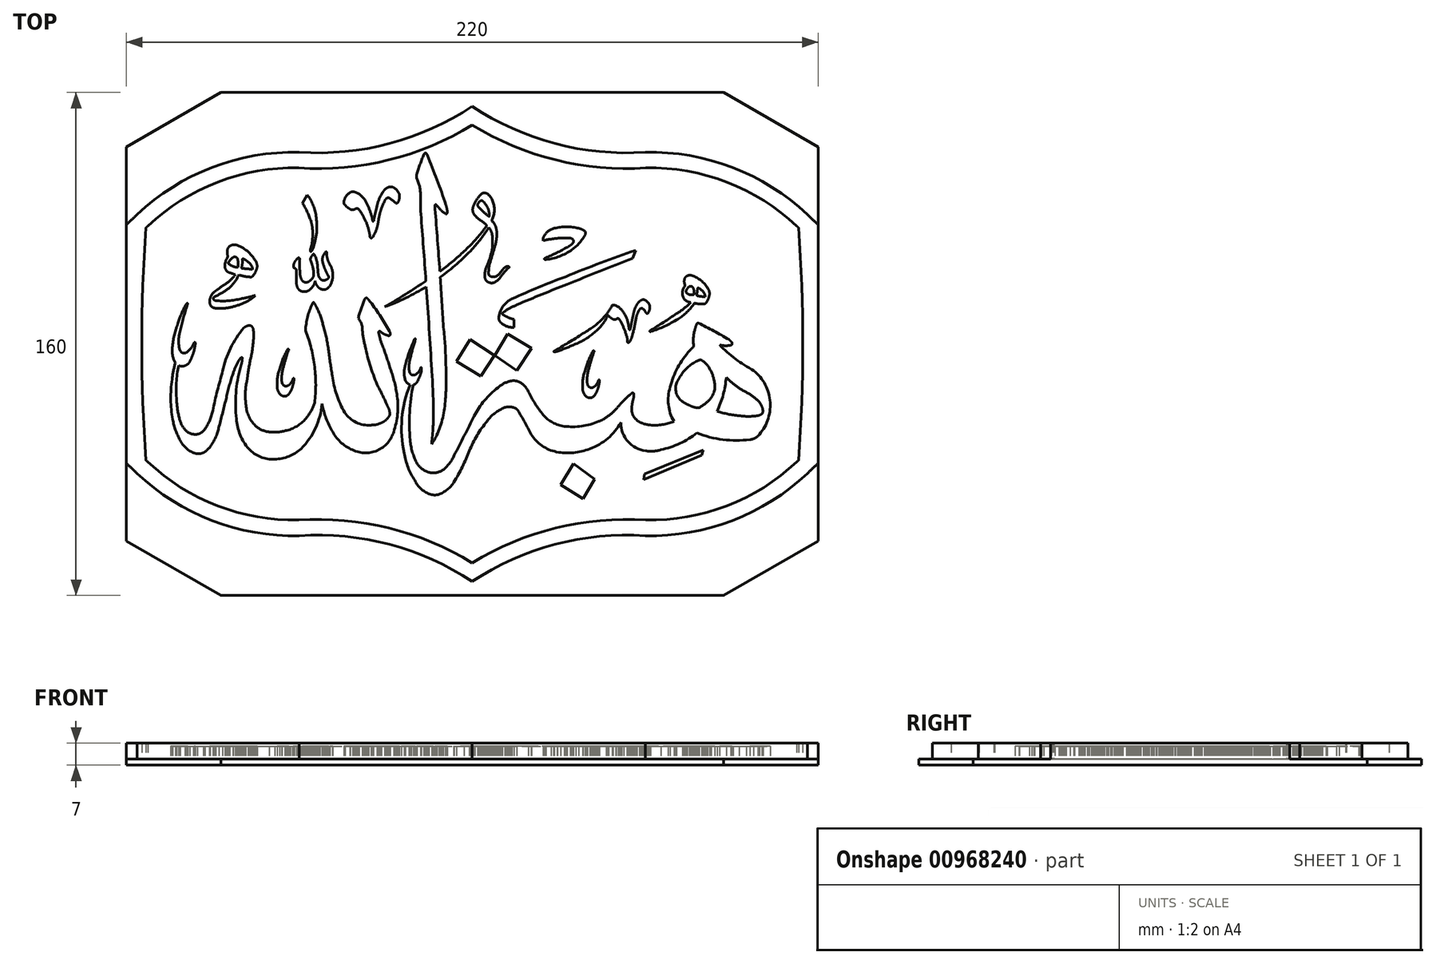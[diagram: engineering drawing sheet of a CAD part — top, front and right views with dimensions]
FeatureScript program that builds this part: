
annotation { "Feature Type Name" : "Feature", "Feature Type Description" : "" }
export const myFeature = defineFeature(function(context is Context, id is Id, definition is map)
    precondition{}
    {
        {
            var Q0;
            Q0=qCreatedBy(makeId("Top.planeOp"),FACE);
            var sketch = newSketch(context, id + "F0", { "sketchPlane" : qUnion([Q0])});
            skLineSegment(sketch, "E0.bottom", {"start": v(-104.12, 78.93) * mm, "end": v(115.88, 78.93) * mm});
            skLineSegment(sketch, "E0.top", {"start": v(-104.12, -81.07) * mm, "end": v(115.88, -81.07) * mm});
            skLineSegment(sketch, "E0.left", {"start": v(-104.12, 78.93) * mm, "end": v(-104.12, -81.07) * mm});
            skLineSegment(sketch, "E0.right", {"start": v(115.88, 78.93) * mm, "end": v(115.88, -81.07) * mm});
            skSolve(sketch);
        }
        {
            var Q0;
            Q0 = qSketchRegion(id + "F0", true);
            extrude(context, id + "F1", {"entities" : qUnion([Q0]), "oppositeDirection" : true, "depth" : 2 * mm, "offsetDistance" : 25 * mm});
        }
        {
            var Q0;
            Q0=makeQuery(id+"F1.opExtrude","CAP_FACE",FACE,{"disambiguationData":[OSD([sQuery(id+"F0.wireOp",EDGE,"E0.bottom"),sQuery(id+"F0.wireOp",EDGE,"E0.top"),sQuery(id+"F0.wireOp",EDGE,"E0.left"),sQuery(id+"F0.wireOp",EDGE,"E0.right")])],"isStart":true});
            var sketch = newSketch(context, id + "F2", { "sketchPlane" : qUnion([Q0])});
            skArc(sketch, "E1", {"start": v(87.55, 0.3) * mm, "mid": v(82.74, 3.05) * mm, "end": v(77.8, 5.57) * mm});
            skArc(sketch, "E2", {"start": v(88.37, -0.47) * mm, "mid": v(88.17, -0.23) * mm, "end": v(87.95, 0) * mm});
            skArc(sketch, "E3", {"start": v(88.17, -1.46) * mm, "mid": v(88.52, -1.04) * mm, "end": v(88.4, -0.5) * mm});
            skArc(sketch, "E4", {"start": v(84.5, -1.3) * mm, "mid": v(86.32, -1.62) * mm, "end": v(88.17, -1.46) * mm});
            skPoint(sketch, "E5.visualSharp", {"position": v(88.39, -0.49) * mm});
            skArc(sketch, "E5.filletArc", {"start": v(88.37, -0.47) * mm, "mid": v(88.38, -0.48) * mm, "end": v(88.4, -0.5) * mm});
            skPoint(sketch, "E6.visualSharp", {"position": v(87.75, 0.19) * mm});
            skArc(sketch, "E6.filletArc", {"start": v(87.95, 0) * mm, "mid": v(87.76, 0.17) * mm, "end": v(87.55, 0.3) * mm});
            skArc(sketch, "E7", {"start": v(84.5, -1.3) * mm, "mid": v(89.64, -5.83) * mm, "end": v(95.4, -9.52) * mm});
            skArc(sketch, "E8", {"start": v(96.73, -30.37) * mm, "mid": v(100.63, -19.66) * mm, "end": v(95.4, -9.52) * mm});
            skArc(sketch, "E9", {"start": v(94.18, -31.5) * mm, "mid": v(95.5, -31.19) * mm, "end": v(96.63, -30.46) * mm});
            skArc(sketch, "E10", {"start": v(77.35, -29.37) * mm, "mid": v(85.63, -31.5) * mm, "end": v(94.18, -31.5) * mm});
            skPoint(sketch, "E11.visualSharp", {"position": v(96.69, -30.4) * mm});
            skArc(sketch, "E11.filletArc", {"start": v(96.63, -30.46) * mm, "mid": v(96.68, -30.41) * mm, "end": v(96.73, -30.37) * mm});
            skArc(sketch, "E12", {"start": v(65.9, -34.73) * mm, "mid": v(71.92, -32.7) * mm, "end": v(77.35, -29.37) * mm});
            skArc(sketch, "E13", {"start": v(61.07, -35.07) * mm, "mid": v(63.5, -35.19) * mm, "end": v(65.9, -34.73) * mm});
            skArc(sketch, "E14", {"start": v(53.13, -26.05) * mm, "mid": v(55.36, -32.08) * mm, "end": v(61.07, -35.07) * mm});
            skArc(sketch, "E15", {"start": v(43.34, -34.38) * mm, "mid": v(49, -31.11) * mm, "end": v(53.13, -26.05) * mm});
            skArc(sketch, "E16", {"start": v(32.67, -35.4) * mm, "mid": v(38.08, -35.68) * mm, "end": v(43.34, -34.38) * mm});
            skArc(sketch, "E17", {"start": v(24.64, -29.8) * mm, "mid": v(28.07, -33.44) * mm, "end": v(32.67, -35.4) * mm});
            skArc(sketch, "E18", {"start": v(24.64, -29.8) * mm, "mid": v(22.58, -25.96) * mm, "end": v(20.37, -22.21) * mm});
            skArc(sketch, "E19", {"start": v(19.47, -21.43) * mm, "mid": v(17.35, -21.06) * mm, "end": v(15.29, -21.72) * mm});
            skPoint(sketch, "E20.visualSharp", {"position": v(20.09, -21.76) * mm});
            skArc(sketch, "E20.filletArc", {"start": v(20.37, -22.21) * mm, "mid": v(19.98, -21.75) * mm, "end": v(19.47, -21.43) * mm});
            skArc(sketch, "E21", {"start": v(15.13, -21.8) * mm, "mid": v(12.63, -23.44) * mm, "end": v(10.6, -25.64) * mm});
            skPoint(sketch, "E22.visualSharp", {"position": v(15.22, -21.76) * mm});
            skArc(sketch, "E22.filletArc", {"start": v(15.13, -21.8) * mm, "mid": v(15.2, -21.76) * mm, "end": v(15.29, -21.72) * mm});
            skArc(sketch, "E23", {"start": v(10.6, -25.64) * mm, "mid": v(7.43, -30.14) * mm, "end": v(4.98, -35.06) * mm});
            skArc(sketch, "E24", {"start": v(0.03, -45.08) * mm, "mid": v(2.73, -40.18) * mm, "end": v(4.98, -35.06) * mm});
            skArc(sketch, "E25", {"start": v(-4.78, -48.95) * mm, "mid": v(-2.07, -47.4) * mm, "end": v(0.03, -45.08) * mm});
            skArc(sketch, "E26", {"start": v(-7.84, -48.76) * mm, "mid": v(-6.32, -49.1) * mm, "end": v(-4.78, -48.95) * mm});
            skArc(sketch, "E27", {"start": v(-12.37, -44.5) * mm, "mid": v(-10.52, -47.06) * mm, "end": v(-7.84, -48.76) * mm});
            skArc(sketch, "E28", {"start": v(-15.76, -35.82) * mm, "mid": v(-14.54, -40.34) * mm, "end": v(-12.37, -44.5) * mm});
            skArc(sketch, "E29", {"start": v(-13.88, -14.04) * mm, "mid": v(-16.5, -24.78) * mm, "end": v(-15.76, -35.82) * mm});
            skArc(sketch, "E30", {"start": v(-12.91, -14.04) * mm, "mid": v(-14.05, -22.82) * mm, "end": v(-13.88, -31.68) * mm});
            skArc(sketch, "E31", {"start": v(-13.88, -31.68) * mm, "mid": v(-13.2, -35.34) * mm, "end": v(-11.83, -38.8) * mm});
            skArc(sketch, "E32", {"start": v(-11.83, -38.8) * mm, "mid": v(-10.17, -40.72) * mm, "end": v(-7.92, -41.89) * mm});
            skArc(sketch, "E33", {"start": v(-7.92, -41.89) * mm, "mid": v(-5.67, -42.02) * mm, "end": v(-3.57, -41.21) * mm});
            skArc(sketch, "E34", {"start": v(-3.57, -41.21) * mm, "mid": v(-1.39, -39.11) * mm, "end": v(0.12, -36.5) * mm});
            skArc(sketch, "E35", {"start": v(0.12, -36.5) * mm, "mid": v(3.34, -30.27) * mm, "end": v(6.43, -24) * mm});
            skArc(sketch, "E36", {"start": v(14.07, -14.96) * mm, "mid": v(9.76, -19.06) * mm, "end": v(6.43, -24) * mm});
            skArc(sketch, "E37", {"start": v(18.04, -12.86) * mm, "mid": v(15.91, -13.65) * mm, "end": v(14.07, -14.96) * mm});
            skArc(sketch, "E38", {"start": v(20, -12.86) * mm, "mid": v(19.02, -12.76) * mm, "end": v(18.04, -12.86) * mm});
            skArc(sketch, "E39", {"start": v(23.7, -16.2) * mm, "mid": v(22.24, -14.1) * mm, "end": v(20, -12.86) * mm});
            skArc(sketch, "E40", {"start": v(23.7, -16.2) * mm, "mid": v(25.88, -20.07) * mm, "end": v(28.48, -23.66) * mm});
            skArc(sketch, "E41", {"start": v(28.48, -23.66) * mm, "mid": v(31.47, -26.06) * mm, "end": v(35.1, -27.27) * mm});
            skArc(sketch, "E42", {"start": v(35.1, -27.27) * mm, "mid": v(40.7, -27.2) * mm, "end": v(46.1, -25.73) * mm});
            skArc(sketch, "E43", {"start": v(46.1, -25.73) * mm, "mid": v(47.63, -25.01) * mm, "end": v(49.03, -24.08) * mm});
            skArc(sketch, "E44", {"start": v(49.03, -24.08) * mm, "mid": v(50.8, -22.64) * mm, "end": v(52.33, -20.96) * mm});
            skArc(sketch, "E45", {"start": v(56.14, -17.16) * mm, "mid": v(54.15, -18.98) * mm, "end": v(52.33, -20.96) * mm});
            skArc(sketch, "E46", {"start": v(56.66, -16.72) * mm, "mid": v(56.4, -16.93) * mm, "end": v(56.14, -17.16) * mm});
            skArc(sketch, "E47", {"start": v(57.07, -16.66) * mm, "mid": v(56.86, -16.63) * mm, "end": v(56.66, -16.72) * mm});
            skArc(sketch, "E48", {"start": v(57.27, -16.98) * mm, "mid": v(57.22, -16.79) * mm, "end": v(57.07, -16.66) * mm});
            skArc(sketch, "E49", {"start": v(57.12, -18.64) * mm, "mid": v(57.26, -17.82) * mm, "end": v(57.27, -16.98) * mm});
            skArc(sketch, "E50", {"start": v(57.12, -18.64) * mm, "mid": v(56.72, -20.33) * mm, "end": v(56.61, -22.06) * mm});
            skArc(sketch, "E51", {"start": v(56.61, -22.06) * mm, "mid": v(56.83, -23.28) * mm, "end": v(57.4, -24.37) * mm});
            skArc(sketch, "E52", {"start": v(57.4, -24.37) * mm, "mid": v(58.21, -25.3) * mm, "end": v(59.23, -25.97) * mm});
            skArc(sketch, "E53", {"start": v(59.23, -25.97) * mm, "mid": v(60.8, -26.56) * mm, "end": v(62.45, -26.84) * mm});
            skArc(sketch, "E54", {"start": v(62.45, -26.84) * mm, "mid": v(66.32, -26.75) * mm, "end": v(70.03, -25.68) * mm});
            skArc(sketch, "E55", {"start": v(68.83, -14.8) * mm, "mid": v(68.28, -20.36) * mm, "end": v(70.03, -25.68) * mm});
            skArc(sketch, "E56", {"start": v(75.09, -3.13) * mm, "mid": v(71.25, -8.58) * mm, "end": v(68.83, -14.8) * mm});
            skArc(sketch, "E57", {"start": v(76.33, -1.87) * mm, "mid": v(75.7, -2.48) * mm, "end": v(75.09, -3.13) * mm});
            skArc(sketch, "E58", {"start": v(76.74, 3.66) * mm, "mid": v(76.23, 0.92) * mm, "end": v(76.33, -1.87) * mm});
            skArc(sketch, "E59", {"start": v(77.32, 5.35) * mm, "mid": v(77, 4.52) * mm, "end": v(76.74, 3.66) * mm});
            skArc(sketch, "E60", {"start": v(77.8, 5.57) * mm, "mid": v(77.51, 5.57) * mm, "end": v(77.32, 5.35) * mm});
            skArc(sketch, "E61", {"start": v(77.95, -6.25) * mm, "mid": v(74.7, -8.26) * mm, "end": v(72.19, -11.13) * mm});
            skArc(sketch, "E62", {"start": v(72.14, -11.2) * mm, "mid": v(71.55, -12.18) * mm, "end": v(71.03, -13.2) * mm});
            skPoint(sketch, "E63.visualSharp", {"position": v(76.34, -7.08) * mm});
            skArc(sketch, "E63.filletArc", {"start": v(72.14, -11.2) * mm, "mid": v(72.17, -11.16) * mm, "end": v(72.19, -11.13) * mm});
            skArc(sketch, "E64", {"start": v(72.68, -19.35) * mm, "mid": v(73.84, -20.07) * mm, "end": v(75.08, -20.64) * mm});
            skPoint(sketch, "E65.visualSharp", {"position": v(69.96, -16.58) * mm});
            skArc(sketch, "E65.filletArc", {"start": v(71.03, -13.2) * mm, "mid": v(70.75, -16.57) * mm, "end": v(72.68, -19.35) * mm});
            skArc(sketch, "E66", {"start": v(75.08, -20.64) * mm, "mid": v(76.06, -21.05) * mm, "end": v(77.08, -21.32) * mm});
            skArc(sketch, "E67", {"start": v(77.08, -21.32) * mm, "mid": v(77.57, -21.4) * mm, "end": v(78.06, -21.32) * mm});
            skArc(sketch, "E68", {"start": v(78.06, -21.32) * mm, "mid": v(80.11, -19.96) * mm, "end": v(81.86, -18.23) * mm});
            skArc(sketch, "E69", {"start": v(81.86, -18.23) * mm, "mid": v(83, -15.51) * mm, "end": v(82.8, -12.58) * mm});
            skArc(sketch, "E70", {"start": v(82.69, -12.2) * mm, "mid": v(81.85, -9.8) * mm, "end": v(80.5, -7.67) * mm});
            skPoint(sketch, "E71.visualSharp", {"position": v(82.73, -12.4) * mm});
            skArc(sketch, "E71.filletArc", {"start": v(82.69, -12.2) * mm, "mid": v(82.74, -12.39) * mm, "end": v(82.8, -12.58) * mm});
            skArc(sketch, "E72", {"start": v(80.5, -7.67) * mm, "mid": v(79.76, -6.9) * mm, "end": v(78.91, -6.25) * mm});
            skArc(sketch, "E73", {"start": v(78.91, -6.25) * mm, "mid": v(78.43, -6.15) * mm, "end": v(77.95, -6.25) * mm});
            skArc(sketch, "E74", {"start": v(83.78, -22.45) * mm, "mid": v(85.72, -17.22) * mm, "end": v(86.66, -11.72) * mm});
            skArc(sketch, "E75", {"start": v(83.78, -22.45) * mm, "mid": v(87.22, -23.38) * mm, "end": v(90.75, -23.88) * mm});
            skArc(sketch, "E76", {"start": v(90.75, -23.88) * mm, "mid": v(93.72, -24.1) * mm, "end": v(96.7, -23.88) * mm});
            skArc(sketch, "E77", {"start": v(96.7, -23.88) * mm, "mid": v(97.4, -23.67) * mm, "end": v(98.01, -23.29) * mm});
            skArc(sketch, "E78", {"start": v(98.01, -23.29) * mm, "mid": v(98.17, -23.12) * mm, "end": v(98.3, -22.94) * mm});
            skArc(sketch, "E79", {"start": v(98.3, -22.94) * mm, "mid": v(98.34, -22.43) * mm, "end": v(98.3, -21.92) * mm});
            skArc(sketch, "E80", {"start": v(98.3, -21.92) * mm, "mid": v(97.87, -20.67) * mm, "end": v(97.2, -19.52) * mm});
            skArc(sketch, "E81", {"start": v(97.2, -19.52) * mm, "mid": v(95.27, -17.82) * mm, "end": v(93.1, -16.44) * mm});
            skArc(sketch, "E82", {"start": v(88.9, -13.7) * mm, "mid": v(90.91, -15.2) * mm, "end": v(93.1, -16.44) * mm});
            skArc(sketch, "E83", {"start": v(86.66, -11.72) * mm, "mid": v(87.73, -12.76) * mm, "end": v(88.9, -13.7) * mm});
            skArc(sketch, "E84", {"start": v(-15.4, -12.66) * mm, "mid": v(-14.79, -13.51) * mm, "end": v(-13.88, -14.04) * mm});
            skArc(sketch, "E85", {"start": v(-15.4, -7.76) * mm, "mid": v(-15.8, -10.2) * mm, "end": v(-15.4, -12.66) * mm});
            skArc(sketch, "E86", {"start": v(-12.42, 0.48) * mm, "mid": v(-14.13, -3.56) * mm, "end": v(-15.4, -7.76) * mm});
            skArc(sketch, "E87", {"start": v(-12.28, 0.65) * mm, "mid": v(-12.37, 0.58) * mm, "end": v(-12.42, 0.48) * mm});
            skArc(sketch, "E88", {"start": v(-12.16, 0.51) * mm, "mid": v(-12.2, 0.6) * mm, "end": v(-12.28, 0.65) * mm});
            skArc(sketch, "E89", {"start": v(-12.16, 0.51) * mm, "mid": v(-13.08, -2.52) * mm, "end": v(-13.84, -5.6) * mm});
            skArc(sketch, "E90", {"start": v(-13.84, -5.6) * mm, "mid": v(-14.19, -7.54) * mm, "end": v(-14.18, -9.5) * mm});
            skArc(sketch, "E91", {"start": v(-14.18, -9.5) * mm, "mid": v(-14.05, -10.07) * mm, "end": v(-13.75, -10.59) * mm});
            skArc(sketch, "E92", {"start": v(-13.75, -10.59) * mm, "mid": v(-13.63, -10.74) * mm, "end": v(-13.48, -10.87) * mm});
            skArc(sketch, "E93", {"start": v(-13.48, -10.87) * mm, "mid": v(-12.86, -10.98) * mm, "end": v(-12.25, -10.87) * mm});
            skArc(sketch, "E94", {"start": v(-12.25, -10.87) * mm, "mid": v(-11.26, -10) * mm, "end": v(-10.58, -8.87) * mm});
            skArc(sketch, "E95", {"start": v(-12.91, -14.04) * mm, "mid": v(-12.26, -13.8) * mm, "end": v(-11.77, -13.3) * mm});
            skArc(sketch, "E96", {"start": v(-11.77, -13.3) * mm, "mid": v(-11, -11.9) * mm, "end": v(-10.47, -10.4) * mm});
            skArc(sketch, "E97", {"start": v(-10.47, -10.4) * mm, "mid": v(-10.31, -9.76) * mm, "end": v(-10.27, -9.1) * mm});
            skArc(sketch, "E98", {"start": v(-10.58, -8.87) * mm, "mid": v(-10.5, -8.65) * mm, "end": v(-10.44, -8.43) * mm});
            skArc(sketch, "E99", {"start": v(-10.27, -9.1) * mm, "mid": v(-10.3, -8.75) * mm, "end": v(-10.44, -8.43) * mm});
            skArc(sketch, "E100", {"start": v(-2.52, 43.23) * mm, "mid": v(-5.32, 51.16) * mm, "end": v(-8.41, 58.98) * mm});
            skArc(sketch, "E101", {"start": v(-2.1, 41.5) * mm, "mid": v(-2.27, 42.37) * mm, "end": v(-2.52, 43.23) * mm});
            skArc(sketch, "E102", {"start": v(-2.1, 40.63) * mm, "mid": v(-2.09, 41.06) * mm, "end": v(-2.1, 41.5) * mm});
            skArc(sketch, "E103", {"start": v(-2.2, 40.37) * mm, "mid": v(-2.13, 40.5) * mm, "end": v(-2.1, 40.63) * mm});
            skArc(sketch, "E104", {"start": v(-2.34, 40.3) * mm, "mid": v(-2.26, 40.32) * mm, "end": v(-2.2, 40.37) * mm});
            skArc(sketch, "E105", {"start": v(-2.56, 40.33) * mm, "mid": v(-2.45, 40.3) * mm, "end": v(-2.34, 40.3) * mm});
            skArc(sketch, "E106", {"start": v(-4.02, 41.47) * mm, "mid": v(-3.34, 40.84) * mm, "end": v(-2.56, 40.33) * mm});
            skArc(sketch, "E107", {"start": v(-5.38, 43) * mm, "mid": v(-4.72, 42.22) * mm, "end": v(-4.02, 41.47) * mm});
            skArc(sketch, "E108", {"start": v(-5.38, 43) * mm, "mid": v(-5.47, 43.12) * mm, "end": v(-5.57, 43.22) * mm});
            skArc(sketch, "E109", {"start": v(-5.57, 43.22) * mm, "mid": v(-5.66, 43.27) * mm, "end": v(-5.76, 43.3) * mm});
            skArc(sketch, "E110", {"start": v(-5.76, 43.3) * mm, "mid": v(-5.91, 43.24) * mm, "end": v(-5.98, 43.1) * mm});
            skArc(sketch, "E111", {"start": v(-5.98, 43.1) * mm, "mid": v(-5.98, 43.07) * mm, "end": v(-5.98, 43.05) * mm});
            skArc(sketch, "E112", {"start": v(-5.98, 43.05) * mm, "mid": v(-5.98, 42.64) * mm, "end": v(-5.98, 42.22) * mm});
            skArc(sketch, "E113", {"start": v(-3.28, 4.32) * mm, "mid": v(-4.52, 23.12) * mm, "end": v(-5.96, 41.9) * mm});
            skPoint(sketch, "E114.visualSharp", {"position": v(-5.98, 42.05) * mm});
            skArc(sketch, "E114.filletArc", {"start": v(-5.98, 42.22) * mm, "mid": v(-5.97, 42.06) * mm, "end": v(-5.96, 41.9) * mm});
            skArc(sketch, "E115", {"start": v(-2.53, -7.79) * mm, "mid": v(-2.75, -1.73) * mm, "end": v(-3.28, 4.32) * mm});
            skArc(sketch, "E116", {"start": v(-2.67, -18.59) * mm, "mid": v(-2.4, -13.2) * mm, "end": v(-2.53, -7.79) * mm});
            skArc(sketch, "E117", {"start": v(-5.44, -30.1) * mm, "mid": v(-3.51, -24.48) * mm, "end": v(-2.67, -18.59) * mm});
            skArc(sketch, "E118", {"start": v(-7.04, -32.9) * mm, "mid": v(-6.15, -31.55) * mm, "end": v(-5.44, -30.1) * mm});
            skArc(sketch, "E119", {"start": v(-7.04, -32.9) * mm, "mid": v(-6.57, -27.35) * mm, "end": v(-6.45, -21.8) * mm});
            skArc(sketch, "E120", {"start": v(-6.46, -21.5) * mm, "mid": v(-6.67, -15.4) * mm, "end": v(-7, -9.3) * mm});
            skPoint(sketch, "E121.visualSharp", {"position": v(-6.45, -21.64) * mm});
            skArc(sketch, "E121.filletArc", {"start": v(-6.45, -21.8) * mm, "mid": v(-6.45, -21.65) * mm, "end": v(-6.46, -21.5) * mm});
            skArc(sketch, "E122", {"start": v(-7, -9.3) * mm, "mid": v(-8.62, 15.47) * mm, "end": v(-10.46, 40.23) * mm});
            skArc(sketch, "E123", {"start": v(-10.57, 43) * mm, "mid": v(-10.54, 41.61) * mm, "end": v(-10.46, 40.23) * mm});
            skArc(sketch, "E124", {"start": v(-10.57, 43) * mm, "mid": v(-10.55, 44.49) * mm, "end": v(-10.57, 45.97) * mm});
            skArc(sketch, "E125", {"start": v(-10.57, 45.97) * mm, "mid": v(-10.87, 48.96) * mm, "end": v(-11.83, 51.8) * mm});
            skArc(sketch, "E126", {"start": v(-11.83, 52.73) * mm, "mid": v(-11.89, 52.27) * mm, "end": v(-11.83, 51.8) * mm});
            skArc(sketch, "E127", {"start": v(-9.5, 59.16) * mm, "mid": v(-10.76, 55.99) * mm, "end": v(-11.83, 52.73) * mm});
            skArc(sketch, "E128", {"start": v(-8.41, 58.98) * mm, "mid": v(-8.53, 59.22) * mm, "end": v(-8.65, 59.44) * mm});
            skArc(sketch, "E129", {"start": v(-8.65, 59.44) * mm, "mid": v(-8.8, 59.6) * mm, "end": v(-9, 59.7) * mm});
            skArc(sketch, "E130", {"start": v(-9.32, 59.53) * mm, "mid": v(-9.41, 59.35) * mm, "end": v(-9.5, 59.16) * mm});
            skArc(sketch, "E131", {"start": v(-9.15, 59.69) * mm, "mid": v(-9.24, 59.62) * mm, "end": v(-9.32, 59.53) * mm});
            skArc(sketch, "E132", {"start": v(-9, 59.7) * mm, "mid": v(-9.08, 59.7) * mm, "end": v(-9.15, 59.69) * mm});
            skArc(sketch, "E133", {"start": v(-20.48, 3.04) * mm, "mid": v(-23.56, 8.11) * mm, "end": v(-27.02, 12.94) * mm});
            skArc(sketch, "E134", {"start": v(-20.22, 1.9) * mm, "mid": v(-20.24, 2.5) * mm, "end": v(-20.48, 3.04) * mm});
            skArc(sketch, "E135", {"start": v(-20.45, 1.6) * mm, "mid": v(-20.3, 1.73) * mm, "end": v(-20.22, 1.9) * mm});
            skArc(sketch, "E136", {"start": v(-20.98, 1.6) * mm, "mid": v(-20.72, 1.56) * mm, "end": v(-20.45, 1.6) * mm});
            skArc(sketch, "E137", {"start": v(-23.06, 2.68) * mm, "mid": v(-22.07, 2.05) * mm, "end": v(-20.98, 1.6) * mm});
            skArc(sketch, "E138", {"start": v(-23.06, 2.68) * mm, "mid": v(-23.22, 2.82) * mm, "end": v(-23.4, 2.94) * mm});
            skArc(sketch, "E139", {"start": v(-23.4, 2.94) * mm, "mid": v(-23.56, 2.97) * mm, "end": v(-23.73, 2.94) * mm});
            skArc(sketch, "E140", {"start": v(-23.73, 2.94) * mm, "mid": v(-23.82, 2.87) * mm, "end": v(-23.88, 2.77) * mm});
            skArc(sketch, "E141", {"start": v(-23.88, 2.77) * mm, "mid": v(-23.91, 2.57) * mm, "end": v(-23.88, 2.37) * mm});
            skArc(sketch, "E142", {"start": v(-23.88, 2.37) * mm, "mid": v(-23.34, 0.3) * mm, "end": v(-22.65, -1.72) * mm});
            skArc(sketch, "E143", {"start": v(-20.18, -8.93) * mm, "mid": v(-21.36, -5.3) * mm, "end": v(-22.65, -1.72) * mm});
            skArc(sketch, "E144", {"start": v(-18.01, -17.66) * mm, "mid": v(-18.87, -13.24) * mm, "end": v(-20.18, -8.93) * mm});
            skArc(sketch, "E145", {"start": v(-19.12, -29.05) * mm, "mid": v(-17.9, -23.42) * mm, "end": v(-18.01, -17.66) * mm});
            skArc(sketch, "E146", {"start": v(-23.35, -34.48) * mm, "mid": v(-20.72, -32.17) * mm, "end": v(-19.12, -29.05) * mm});
            skArc(sketch, "E147", {"start": v(-31.72, -34.96) * mm, "mid": v(-27.48, -35.7) * mm, "end": v(-23.35, -34.48) * mm});
            skArc(sketch, "E148", {"start": v(-38.56, -29.02) * mm, "mid": v(-35.67, -32.6) * mm, "end": v(-31.72, -34.96) * mm});
            skArc(sketch, "E149", {"start": v(-41.89, -20.1) * mm, "mid": v(-40.6, -24.7) * mm, "end": v(-38.56, -29.02) * mm});
            skArc(sketch, "E150", {"start": v(-48.57, -34.38) * mm, "mid": v(-43.98, -27.83) * mm, "end": v(-41.89, -20.1) * mm});
            skArc(sketch, "E151", {"start": v(-56.97, -37.73) * mm, "mid": v(-52.46, -36.83) * mm, "end": v(-48.57, -34.38) * mm});
            skArc(sketch, "E152", {"start": v(-65.23, -34.38) * mm, "mid": v(-61.49, -37) * mm, "end": v(-56.97, -37.73) * mm});
            skArc(sketch, "E153", {"start": v(-69.13, -24.94) * mm, "mid": v(-67.94, -29.97) * mm, "end": v(-65.23, -34.38) * mm});
            skArc(sketch, "E154", {"start": v(-67.84, -8.54) * mm, "mid": v(-69.28, -16.68) * mm, "end": v(-69.13, -24.94) * mm});
            skArc(sketch, "E155", {"start": v(-67.55, -7.48) * mm, "mid": v(-67.7, -8) * mm, "end": v(-67.84, -8.54) * mm});
            skArc(sketch, "E156", {"start": v(-67.55, -7.48) * mm, "mid": v(-67.43, -7.02) * mm, "end": v(-67.37, -6.56) * mm});
            skArc(sketch, "E157", {"start": v(-67.26, -5.55) * mm, "mid": v(-67.31, -6.05) * mm, "end": v(-67.37, -6.56) * mm});
            skArc(sketch, "E158", {"start": v(-67.26, -5.55) * mm, "mid": v(-67.28, -5.43) * mm, "end": v(-67.37, -5.36) * mm});
            skArc(sketch, "E159", {"start": v(-67.37, -5.36) * mm, "mid": v(-67.46, -5.33) * mm, "end": v(-67.56, -5.36) * mm});
            skArc(sketch, "E160", {"start": v(-67.56, -5.36) * mm, "mid": v(-67.64, -5.41) * mm, "end": v(-67.72, -5.49) * mm});
            skArc(sketch, "E161", {"start": v(-67.72, -5.49) * mm, "mid": v(-68.12, -5.97) * mm, "end": v(-68.46, -6.5) * mm});
            skArc(sketch, "E162", {"start": v(-68.46, -6.5) * mm, "mid": v(-69.47, -8.51) * mm, "end": v(-70.25, -10.64) * mm});
            skArc(sketch, "E163", {"start": v(-70.25, -10.64) * mm, "mid": v(-71.48, -14.6) * mm, "end": v(-72.46, -18.63) * mm});
            skArc(sketch, "E164", {"start": v(-74.8, -27.88) * mm, "mid": v(-73.61, -23.26) * mm, "end": v(-72.46, -18.63) * mm});
            skArc(sketch, "E165", {"start": v(-77.8, -34.12) * mm, "mid": v(-76, -31.32) * mm, "end": v(-74.88, -28.2) * mm});
            skPoint(sketch, "E166.visualSharp", {"position": v(-74.85, -28.07) * mm});
            skArc(sketch, "E166.filletArc", {"start": v(-74.8, -27.88) * mm, "mid": v(-74.84, -28.04) * mm, "end": v(-74.88, -28.2) * mm});
            skArc(sketch, "E167", {"start": v(-79.7, -35.69) * mm, "mid": v(-78.69, -34.98) * mm, "end": v(-77.8, -34.12) * mm});
            skArc(sketch, "E168", {"start": v(-82.78, -35.69) * mm, "mid": v(-81.24, -36) * mm, "end": v(-79.7, -35.69) * mm});
            skArc(sketch, "E169", {"start": v(-87.04, -31.73) * mm, "mid": v(-85.28, -34.11) * mm, "end": v(-82.78, -35.69) * mm});
            skArc(sketch, "E170", {"start": v(-89.39, -25.08) * mm, "mid": v(-88.5, -28.5) * mm, "end": v(-87.04, -31.73) * mm});
            skArc(sketch, "E171", {"start": v(-89.6, -12.35) * mm, "mid": v(-90.04, -18.72) * mm, "end": v(-89.39, -25.08) * mm});
            skArc(sketch, "E172", {"start": v(-88.57, -7.07) * mm, "mid": v(-89.2, -9.69) * mm, "end": v(-89.6, -12.35) * mm});
            skArc(sketch, "E173", {"start": v(-87.54, -7.94) * mm, "mid": v(-88.26, -13.42) * mm, "end": v(-88.15, -18.94) * mm});
            skArc(sketch, "E174", {"start": v(-88.15, -18.94) * mm, "mid": v(-87.86, -22) * mm, "end": v(-87.22, -25) * mm});
            skArc(sketch, "E175", {"start": v(-87.22, -25) * mm, "mid": v(-86.47, -26.89) * mm, "end": v(-85.28, -28.54) * mm});
            skArc(sketch, "E176", {"start": v(-85.28, -28.54) * mm, "mid": v(-83.58, -29.62) * mm, "end": v(-81.57, -29.76) * mm});
            skArc(sketch, "E177", {"start": v(-81.57, -29.76) * mm, "mid": v(-80.24, -29.22) * mm, "end": v(-79.19, -28.23) * mm});
            skArc(sketch, "E178", {"start": v(-79.19, -28.23) * mm, "mid": v(-77.62, -25.37) * mm, "end": v(-76.67, -22.24) * mm});
            skArc(sketch, "E179", {"start": v(-73.5, -9.69) * mm, "mid": v(-75.2, -15.94) * mm, "end": v(-76.67, -22.24) * mm});
            skArc(sketch, "E180", {"start": v(-66.78, 4) * mm, "mid": v(-71, -2.42) * mm, "end": v(-73.5, -9.69) * mm});
            skArc(sketch, "E181", {"start": v(-65.49, 4.77) * mm, "mid": v(-66.19, 4.47) * mm, "end": v(-66.78, 4) * mm});
            skArc(sketch, "E182", {"start": v(-64.61, 4.77) * mm, "mid": v(-65.05, 4.84) * mm, "end": v(-65.49, 4.77) * mm});
            skArc(sketch, "E183", {"start": v(-63.79, 3.7) * mm, "mid": v(-64.1, 4.32) * mm, "end": v(-64.61, 4.77) * mm});
            skArc(sketch, "E184", {"start": v(-63.79, -0.28) * mm, "mid": v(-63.66, 1.7) * mm, "end": v(-63.79, 3.7) * mm});
            skArc(sketch, "E185", {"start": v(-64.36, -4.6) * mm, "mid": v(-64, -2.45) * mm, "end": v(-63.79, -0.28) * mm});
            skArc(sketch, "E186", {"start": v(-64.36, -4.6) * mm, "mid": v(-65.05, -7.88) * mm, "end": v(-65.55, -11.19) * mm});
            skArc(sketch, "E187", {"start": v(-65.84, -12.98) * mm, "mid": v(-66.3, -16.5) * mm, "end": v(-66.15, -20.06) * mm});
            skPoint(sketch, "E188.visualSharp", {"position": v(-65.66, -12.17) * mm});
            skArc(sketch, "E188.filletArc", {"start": v(-65.84, -12.98) * mm, "mid": v(-65.68, -12.09) * mm, "end": v(-65.55, -11.19) * mm});
            skArc(sketch, "E189", {"start": v(-66.15, -20.06) * mm, "mid": v(-65.28, -23.86) * mm, "end": v(-63.12, -27.11) * mm});
            skArc(sketch, "E190", {"start": v(-63.12, -27.11) * mm, "mid": v(-61.05, -28.43) * mm, "end": v(-58.7, -29.07) * mm});
            skArc(sketch, "E191", {"start": v(-58.7, -29.07) * mm, "mid": v(-55.86, -29.09) * mm, "end": v(-53.09, -28.56) * mm});
            skArc(sketch, "E192", {"start": v(-53.09, -28.56) * mm, "mid": v(-49.56, -27.01) * mm, "end": v(-46.75, -24.38) * mm});
            skArc(sketch, "E193", {"start": v(-46.75, -24.38) * mm, "mid": v(-45.3, -22.19) * mm, "end": v(-44.28, -19.76) * mm});
            skArc(sketch, "E194", {"start": v(-44.28, -19.76) * mm, "mid": v(-43.9, -14.07) * mm, "end": v(-44.28, -8.38) * mm});
            skArc(sketch, "E195", {"start": v(-44.28, -8.38) * mm, "mid": v(-45.33, -2.52) * mm, "end": v(-47.18, 3.13) * mm});
            skArc(sketch, "E196", {"start": v(-44.99, 11.7) * mm, "mid": v(-46.5, 7.52) * mm, "end": v(-47.18, 3.13) * mm});
            skArc(sketch, "E197", {"start": v(-44.7, 12.13) * mm, "mid": v(-44.86, 11.93) * mm, "end": v(-44.99, 11.7) * mm});
            skArc(sketch, "E198", {"start": v(-44.6, 12.14) * mm, "mid": v(-44.64, 12.15) * mm, "end": v(-44.7, 12.13) * mm});
            skArc(sketch, "E199", {"start": v(-44.3, 11.84) * mm, "mid": v(-44.44, 12) * mm, "end": v(-44.6, 12.14) * mm});
            skArc(sketch, "E200", {"start": v(-43.64, 10.58) * mm, "mid": v(-43.95, 11.22) * mm, "end": v(-44.3, 11.84) * mm});
            skArc(sketch, "E201", {"start": v(-41.44, 4.4) * mm, "mid": v(-42.33, 7.56) * mm, "end": v(-43.64, 10.58) * mm});
            skArc(sketch, "E202", {"start": v(-39.82, -3.25) * mm, "mid": v(-40.46, 0.6) * mm, "end": v(-41.44, 4.4) * mm});
            skArc(sketch, "E203", {"start": v(-39.82, -3.25) * mm, "mid": v(-39.27, -7.21) * mm, "end": v(-38.65, -11.17) * mm});
            skArc(sketch, "E204", {"start": v(-38.65, -11.17) * mm, "mid": v(-37.23, -17.2) * mm, "end": v(-34.72, -22.88) * mm});
            skArc(sketch, "E205", {"start": v(-34.72, -22.88) * mm, "mid": v(-31.07, -26.01) * mm, "end": v(-26.33, -26.89) * mm});
            skArc(sketch, "E206", {"start": v(-25.65, -26.85) * mm, "mid": v(-24.29, -26.64) * mm, "end": v(-23, -26.14) * mm});
            skPoint(sketch, "E207.visualSharp", {"position": v(-25.97, -26.85) * mm});
            skArc(sketch, "E207.filletArc", {"start": v(-25.65, -26.85) * mm, "mid": v(-26, -26.87) * mm, "end": v(-26.33, -26.89) * mm});
            skArc(sketch, "E208", {"start": v(-23, -26.14) * mm, "mid": v(-22.14, -25.72) * mm, "end": v(-21.4, -25.1) * mm});
            skArc(sketch, "E209", {"start": v(-21.4, -25.1) * mm, "mid": v(-20.75, -24.35) * mm, "end": v(-20.31, -23.48) * mm});
            skArc(sketch, "E210", {"start": v(-20.31, -23.48) * mm, "mid": v(-20.48, -22.3) * mm, "end": v(-20.9, -21.18) * mm});
            skArc(sketch, "E211", {"start": v(-21.46, -19.98) * mm, "mid": v(-22.66, -17.36) * mm, "end": v(-24, -14.8) * mm});
            skPoint(sketch, "E212.visualSharp", {"position": v(-21.13, -20.77) * mm});
            skArc(sketch, "E212.filletArc", {"start": v(-21.46, -19.98) * mm, "mid": v(-21.19, -20.58) * mm, "end": v(-20.9, -21.18) * mm});
            skArc(sketch, "E213", {"start": v(-28.17, -1.8) * mm, "mid": v(-26.44, -8.42) * mm, "end": v(-24, -14.8) * mm});
            skArc(sketch, "E214", {"start": v(-29.06, 3.53) * mm, "mid": v(-28.77, 0.84) * mm, "end": v(-28.17, -1.8) * mm});
            skArc(sketch, "E215", {"start": v(-29.06, 3.53) * mm, "mid": v(-29.4, 5.45) * mm, "end": v(-30.4, 7.12) * mm});
            skArc(sketch, "E216", {"start": v(-28.48, 12.85) * mm, "mid": v(-29.54, 10.02) * mm, "end": v(-30.4, 7.12) * mm});
            skArc(sketch, "E217", {"start": v(-28.17, 13.4) * mm, "mid": v(-28.36, 13.14) * mm, "end": v(-28.48, 12.85) * mm});
            skArc(sketch, "E218", {"start": v(-27.02, 12.94) * mm, "mid": v(-27.22, 13.18) * mm, "end": v(-27.45, 13.4) * mm});
            skArc(sketch, "E219", {"start": v(-27.45, 13.4) * mm, "mid": v(-27.81, 13.55) * mm, "end": v(-28.17, 13.4) * mm});
            skArc(sketch, "E220", {"start": v(-89.56, -3.12) * mm, "mid": v(-89.35, -5.16) * mm, "end": v(-88.57, -7.07) * mm});
            skArc(sketch, "E221", {"start": v(-88.12, 4.32) * mm, "mid": v(-89.13, 0.66) * mm, "end": v(-89.56, -3.12) * mm});
            skArc(sketch, "E222", {"start": v(-85.33, 11.17) * mm, "mid": v(-86.7, 8.38) * mm, "end": v(-87.75, 5.46) * mm});
            skPoint(sketch, "E223.visualSharp", {"position": v(-87.91, 4.88) * mm});
            skArc(sketch, "E223.filletArc", {"start": v(-88.12, 4.32) * mm, "mid": v(-87.93, 4.89) * mm, "end": v(-87.75, 5.46) * mm});
            skArc(sketch, "E224", {"start": v(-84.88, 11.86) * mm, "mid": v(-85.12, 11.53) * mm, "end": v(-85.33, 11.17) * mm});
            skArc(sketch, "E225", {"start": v(-84.76, 11.93) * mm, "mid": v(-84.83, 11.92) * mm, "end": v(-84.88, 11.86) * mm});
            skArc(sketch, "E226", {"start": v(-84.67, 11.88) * mm, "mid": v(-84.7, 11.92) * mm, "end": v(-84.76, 11.93) * mm});
            skArc(sketch, "E227", {"start": v(-84.68, 11.63) * mm, "mid": v(-84.66, 11.75) * mm, "end": v(-84.67, 11.88) * mm});
            skArc(sketch, "E228", {"start": v(-85.2, 9.87) * mm, "mid": v(-84.98, 10.57) * mm, "end": v(-84.78, 11.28) * mm});
            skPoint(sketch, "E229.visualSharp", {"position": v(-84.7, 11.57) * mm});
            skArc(sketch, "E229.filletArc", {"start": v(-84.68, 11.63) * mm, "mid": v(-84.73, 11.46) * mm, "end": v(-84.78, 11.28) * mm});
            skArc(sketch, "E230", {"start": v(-85.2, 9.87) * mm, "mid": v(-86.4, 5.75) * mm, "end": v(-87.37, 1.57) * mm});
            skArc(sketch, "E231", {"start": v(-87.37, 1.57) * mm, "mid": v(-87.5, -0.57) * mm, "end": v(-87.24, -2.7) * mm});
            skArc(sketch, "E232", {"start": v(-87.24, -2.7) * mm, "mid": v(-86.94, -3.34) * mm, "end": v(-86.43, -3.82) * mm});
            skArc(sketch, "E233", {"start": v(-86.43, -3.82) * mm, "mid": v(-85.75, -4.01) * mm, "end": v(-85.07, -3.82) * mm});
            skArc(sketch, "E234", {"start": v(-85.07, -3.82) * mm, "mid": v(-83.78, -2.6) * mm, "end": v(-82.8, -1.1) * mm});
            skArc(sketch, "E235", {"start": v(-82.8, -1.1) * mm, "mid": v(-82.69, -0.87) * mm, "end": v(-82.6, -0.64) * mm});
            skArc(sketch, "E236", {"start": v(-87.54, -7.94) * mm, "mid": v(-86.52, -8.15) * mm, "end": v(-85.5, -7.97) * mm});
            skArc(sketch, "E237", {"start": v(-85.5, -7.97) * mm, "mid": v(-84.6, -7.46) * mm, "end": v(-83.96, -6.64) * mm});
            skArc(sketch, "E238", {"start": v(-83.96, -6.64) * mm, "mid": v(-83.34, -5.36) * mm, "end": v(-82.87, -4.02) * mm});
            skArc(sketch, "E239", {"start": v(-82.87, -4.02) * mm, "mid": v(-82.44, -2.39) * mm, "end": v(-82.2, -0.72) * mm});
            skArc(sketch, "E240", {"start": v(-82.2, -0.72) * mm, "mid": v(-82.36, -0.53) * mm, "end": v(-82.6, -0.64) * mm});
            skArc(sketch, "E241", {"start": v(80.8, 16.62) * mm, "mid": v(78.65, 19.11) * mm, "end": v(75.78, 20.72) * mm});
            skArc(sketch, "E242", {"start": v(81.3, 14.42) * mm, "mid": v(81.28, 15.57) * mm, "end": v(80.8, 16.62) * mm});
            skArc(sketch, "E243", {"start": v(80.25, 12.02) * mm, "mid": v(80.91, 13.16) * mm, "end": v(81.3, 14.42) * mm});
            skArc(sketch, "E244", {"start": v(76.53, 11.9) * mm, "mid": v(77.98, 11.69) * mm, "end": v(79.45, 11.62) * mm});
            skPoint(sketch, "E245.visualSharp", {"position": v(79.93, 11.63) * mm});
            skArc(sketch, "E245.filletArc", {"start": v(79.45, 11.62) * mm, "mid": v(79.9, 11.73) * mm, "end": v(80.25, 12.02) * mm});
            skArc(sketch, "E246", {"start": v(75.78, 20.72) * mm, "mid": v(75, 20.8) * mm, "end": v(74.24, 20.63) * mm});
            skArc(sketch, "E247", {"start": v(74.24, 20.63) * mm, "mid": v(73.72, 20.2) * mm, "end": v(73.42, 19.6) * mm});
            skArc(sketch, "E248", {"start": v(73.42, 19.6) * mm, "mid": v(73.3, 18.85) * mm, "end": v(73.42, 18.1) * mm});
            skArc(sketch, "E249", {"start": v(73.5, 17.37) * mm, "mid": v(73.52, 17.74) * mm, "end": v(73.42, 18.1) * mm});
            skArc(sketch, "E250", {"start": v(73.5, 17.37) * mm, "mid": v(72.75, 15.52) * mm, "end": v(73.1, 13.54) * mm});
            skArc(sketch, "E251", {"start": v(73.1, 13.54) * mm, "mid": v(74.1, 12.58) * mm, "end": v(75.41, 12.18) * mm});
            skArc(sketch, "E252", {"start": v(70.9, 8.6) * mm, "mid": v(73.26, 10.25) * mm, "end": v(75.41, 12.18) * mm});
            skArc(sketch, "E253", {"start": v(62.48, 3.2) * mm, "mid": v(66.72, 5.84) * mm, "end": v(70.9, 8.6) * mm});
            skArc(sketch, "E254", {"start": v(71.3, 6.83) * mm, "mid": v(74.2, 9.07) * mm, "end": v(76.53, 11.9) * mm});
            skArc(sketch, "E255", {"start": v(62.64, 2.86) * mm, "mid": v(67.1, 4.58) * mm, "end": v(71.3, 6.83) * mm});
            skArc(sketch, "E256", {"start": v(62.48, 3.2) * mm, "mid": v(62.37, 2.94) * mm, "end": v(62.64, 2.86) * mm});
            skArc(sketch, "E257", {"start": v(74.87, 17.16) * mm, "mid": v(74.24, 16.48) * mm, "end": v(73.86, 15.64) * mm});
            skArc(sketch, "E258", {"start": v(75.8, 17.16) * mm, "mid": v(75.34, 17.29) * mm, "end": v(74.87, 17.16) * mm});
            skArc(sketch, "E259", {"start": v(76.32, 16.38) * mm, "mid": v(76.12, 16.8) * mm, "end": v(75.8, 17.16) * mm});
            skArc(sketch, "E260", {"start": v(76.38, 14.8) * mm, "mid": v(76.42, 15.6) * mm, "end": v(76.32, 16.38) * mm});
            skArc(sketch, "E261", {"start": v(76.18, 14.57) * mm, "mid": v(76.31, 14.65) * mm, "end": v(76.38, 14.8) * mm});
            skArc(sketch, "E262", {"start": v(73.86, 15.64) * mm, "mid": v(73.85, 15.46) * mm, "end": v(73.94, 15.3) * mm});
            skArc(sketch, "E263", {"start": v(73.94, 15.3) * mm, "mid": v(74.44, 14.88) * mm, "end": v(75.04, 14.61) * mm});
            skArc(sketch, "E264", {"start": v(75.04, 14.61) * mm, "mid": v(75.6, 14.53) * mm, "end": v(76.18, 14.57) * mm});
            skArc(sketch, "E265", {"start": v(77.5, 14.27) * mm, "mid": v(78.71, 14.05) * mm, "end": v(79.94, 13.94) * mm});
            skArc(sketch, "E266", {"start": v(77.34, 14.44) * mm, "mid": v(77.4, 14.33) * mm, "end": v(77.5, 14.27) * mm});
            skArc(sketch, "E267", {"start": v(77.62, 16.72) * mm, "mid": v(77.42, 15.59) * mm, "end": v(77.34, 14.44) * mm});
            skArc(sketch, "E268", {"start": v(77.74, 16.79) * mm, "mid": v(77.66, 16.78) * mm, "end": v(77.62, 16.72) * mm});
            skArc(sketch, "E269", {"start": v(79.72, 14.96) * mm, "mid": v(78.89, 16.04) * mm, "end": v(77.74, 16.79) * mm});
            skArc(sketch, "E270", {"start": v(79.89, 14.53) * mm, "mid": v(79.83, 14.75) * mm, "end": v(79.72, 14.96) * mm});
            skArc(sketch, "E271", {"start": v(79.94, 13.94) * mm, "mid": v(79.93, 14.24) * mm, "end": v(79.89, 14.53) * mm});
            skArc(sketch, "E272", {"start": v(61.02, 9) * mm, "mid": v(60.63, 9.7) * mm, "end": v(60, 10.23) * mm});
            skArc(sketch, "E273", {"start": v(60, 10.23) * mm, "mid": v(59.45, 10.2) * mm, "end": v(59.04, 9.83) * mm});
            skArc(sketch, "E274", {"start": v(59.04, 9.83) * mm, "mid": v(58.4, 8.5) * mm, "end": v(57.96, 7.1) * mm});
            skArc(sketch, "E275", {"start": v(56.82, 1.8) * mm, "mid": v(57.48, 4.43) * mm, "end": v(57.96, 7.1) * mm});
            skArc(sketch, "E276", {"start": v(55.82, -0.47) * mm, "mid": v(56.46, 0.6) * mm, "end": v(56.82, 1.8) * mm});
            skArc(sketch, "E277", {"start": v(55.29, -0.56) * mm, "mid": v(55.57, -0.62) * mm, "end": v(55.82, -0.47) * mm});
            skArc(sketch, "E278", {"start": v(55.2, -0.37) * mm, "mid": v(55.2, 0.44) * mm, "end": v(55.06, 1.24) * mm});
            skPoint(sketch, "E279.visualSharp", {"position": v(55.18, -0.47) * mm});
            skArc(sketch, "E279.filletArc", {"start": v(55.2, -0.37) * mm, "mid": v(55.21, -0.48) * mm, "end": v(55.29, -0.56) * mm});
            skArc(sketch, "E280", {"start": v(55.06, 1.24) * mm, "mid": v(54.33, 3.37) * mm, "end": v(53.41, 5.44) * mm});
            skArc(sketch, "E281", {"start": v(53.41, 5.44) * mm, "mid": v(53.1, 6.1) * mm, "end": v(52.7, 6.73) * mm});
            skArc(sketch, "E282", {"start": v(52.7, 6.73) * mm, "mid": v(52.23, 7.05) * mm, "end": v(51.71, 6.84) * mm});
            skArc(sketch, "E283", {"start": v(50.6, 6.84) * mm, "mid": v(51.15, 6.67) * mm, "end": v(51.71, 6.84) * mm});
            skArc(sketch, "E284", {"start": v(49.26, 7.87) * mm, "mid": v(49.88, 7.29) * mm, "end": v(50.6, 6.84) * mm});
            skArc(sketch, "E285", {"start": v(61.02, 9) * mm, "mid": v(61.21, 8.74) * mm, "end": v(61.47, 8.56) * mm});
            skArc(sketch, "E286", {"start": v(61.47, 8.56) * mm, "mid": v(61.69, 8.62) * mm, "end": v(61.83, 8.8) * mm});
            skArc(sketch, "E287", {"start": v(61.83, 8.8) * mm, "mid": v(62.23, 9.65) * mm, "end": v(62.38, 10.57) * mm});
            skArc(sketch, "E288", {"start": v(62.38, 10.57) * mm, "mid": v(62.25, 11.35) * mm, "end": v(61.86, 12.03) * mm});
            skArc(sketch, "E289", {"start": v(61.86, 12.03) * mm, "mid": v(61.34, 12.54) * mm, "end": v(60.74, 12.95) * mm});
            skArc(sketch, "E290", {"start": v(60.74, 12.95) * mm, "mid": v(60.12, 13.02) * mm, "end": v(59.53, 12.8) * mm});
            skArc(sketch, "E291", {"start": v(59.53, 12.8) * mm, "mid": v(58.81, 12.19) * mm, "end": v(58.24, 11.44) * mm});
            skArc(sketch, "E292", {"start": v(58.24, 11.44) * mm, "mid": v(57.62, 10.13) * mm, "end": v(57.21, 8.73) * mm});
            skArc(sketch, "E293", {"start": v(56.7, 6.36) * mm, "mid": v(56.96, 7.55) * mm, "end": v(57.21, 8.73) * mm});
            skArc(sketch, "E294", {"start": v(56.7, 6.36) * mm, "mid": v(56.4, 4.98) * mm, "end": v(56.13, 3.6) * mm});
            skArc(sketch, "E295", {"start": v(56.03, 3.43) * mm, "mid": v(56.1, 3.5) * mm, "end": v(56.13, 3.6) * mm});
            skArc(sketch, "E296", {"start": v(55.86, 3.43) * mm, "mid": v(55.95, 3.41) * mm, "end": v(56.03, 3.43) * mm});
            skArc(sketch, "E297", {"start": v(55.8, 3.55) * mm, "mid": v(55.82, 3.49) * mm, "end": v(55.86, 3.43) * mm});
            skArc(sketch, "E298", {"start": v(55.8, 3.55) * mm, "mid": v(55.69, 4.3) * mm, "end": v(55.54, 5.05) * mm});
            skArc(sketch, "E299", {"start": v(55.54, 5.05) * mm, "mid": v(55, 7.03) * mm, "end": v(54.06, 8.84) * mm});
            skArc(sketch, "E300", {"start": v(54.06, 8.84) * mm, "mid": v(53, 10.18) * mm, "end": v(51.58, 11.15) * mm});
            skArc(sketch, "E301", {"start": v(51.58, 11.15) * mm, "mid": v(51.01, 11.3) * mm, "end": v(50.43, 11.31) * mm});
            skArc(sketch, "E302", {"start": v(48.48, 8.22) * mm, "mid": v(49.53, 9.72) * mm, "end": v(50.43, 11.31) * mm});
            skArc(sketch, "E303", {"start": v(42.19, 2.94) * mm, "mid": v(45.55, 5.32) * mm, "end": v(48.48, 8.22) * mm});
            skArc(sketch, "E304", {"start": v(32.99, -2.7) * mm, "mid": v(37.63, 0.04) * mm, "end": v(42.19, 2.94) * mm});
            skArc(sketch, "E305", {"start": v(31.88, -3.34) * mm, "mid": v(32.45, -3.04) * mm, "end": v(32.99, -2.7) * mm});
            skArc(sketch, "E306", {"start": v(49.26, 7.87) * mm, "mid": v(49.18, 7.94) * mm, "end": v(49.07, 7.95) * mm});
            skArc(sketch, "E307", {"start": v(49.07, 7.95) * mm, "mid": v(48.94, 7.9) * mm, "end": v(48.86, 7.78) * mm});
            skArc(sketch, "E308", {"start": v(45.44, 3.21) * mm, "mid": v(47.4, 5.31) * mm, "end": v(48.86, 7.78) * mm});
            skArc(sketch, "E309", {"start": v(38.84, -1.06) * mm, "mid": v(42.32, 0.79) * mm, "end": v(45.44, 3.21) * mm});
            skArc(sketch, "E310", {"start": v(32.86, -3.4) * mm, "mid": v(35.88, -2.3) * mm, "end": v(38.84, -1.06) * mm});
            skArc(sketch, "E311", {"start": v(31.95, -3.62) * mm, "mid": v(32.41, -3.55) * mm, "end": v(32.86, -3.4) * mm});
            skArc(sketch, "E312", {"start": v(31.88, -3.34) * mm, "mid": v(31.8, -3.5) * mm, "end": v(31.95, -3.62) * mm});
            skArc(sketch, "E313", {"start": v(44.28, -3.34) * mm, "mid": v(42.82, -6.4) * mm, "end": v(41.74, -9.63) * mm});
            skArc(sketch, "E314", {"start": v(41.74, -9.63) * mm, "mid": v(41.05, -12.62) * mm, "end": v(41.03, -15.68) * mm});
            skArc(sketch, "E315", {"start": v(41.03, -15.68) * mm, "mid": v(41.5, -17.06) * mm, "end": v(42.55, -18.08) * mm});
            skArc(sketch, "E316", {"start": v(42.55, -18.08) * mm, "mid": v(43.3, -18.23) * mm, "end": v(44.05, -18.08) * mm});
            skArc(sketch, "E317", {"start": v(44.05, -18.08) * mm, "mid": v(44.74, -17.45) * mm, "end": v(45.25, -16.68) * mm});
            skArc(sketch, "E318", {"start": v(45.25, -16.68) * mm, "mid": v(45.79, -15.48) * mm, "end": v(46.13, -14.2) * mm});
            skArc(sketch, "E319", {"start": v(46.13, -14.2) * mm, "mid": v(46.24, -13.63) * mm, "end": v(46.33, -13.06) * mm});
            skArc(sketch, "E320", {"start": v(46.33, -13.06) * mm, "mid": v(46.35, -12.82) * mm, "end": v(46.34, -12.57) * mm});
            skArc(sketch, "E321", {"start": v(46.28, -12.49) * mm, "mid": v(46.12, -12.5) * mm, "end": v(46.04, -12.64) * mm});
            skPoint(sketch, "E322.visualSharp", {"position": v(46.33, -12.53) * mm});
            skArc(sketch, "E322.filletArc", {"start": v(46.34, -12.57) * mm, "mid": v(46.32, -12.52) * mm, "end": v(46.28, -12.49) * mm});
            skPoint(sketch, "E323.visualSharp", {"position": v(46.04, -12.65) * mm});
            skArc(sketch, "E323.filletArc", {"start": v(46.03, -12.67) * mm, "mid": v(46.04, -12.65) * mm, "end": v(46.04, -12.64) * mm});
            skArc(sketch, "E324", {"start": v(44.58, -14.74) * mm, "mid": v(45.26, -14.1) * mm, "end": v(45.77, -13.3) * mm});
            skPoint(sketch, "E325.visualSharp", {"position": v(45.83, -13.19) * mm});
            skArc(sketch, "E325.filletArc", {"start": v(45.88, -13.11) * mm, "mid": v(45.83, -13.2) * mm, "end": v(45.77, -13.3) * mm});
            skArc(sketch, "E326", {"start": v(45.88, -13.11) * mm, "mid": v(45.97, -12.9) * mm, "end": v(46.03, -12.67) * mm});
            skArc(sketch, "E327", {"start": v(43.47, -14.94) * mm, "mid": v(44.05, -14.96) * mm, "end": v(44.58, -14.74) * mm});
            skArc(sketch, "E328", {"start": v(42.56, -14) * mm, "mid": v(42.9, -14.58) * mm, "end": v(43.47, -14.94) * mm});
            skArc(sketch, "E329", {"start": v(42.41, -11.94) * mm, "mid": v(42.4, -12.97) * mm, "end": v(42.56, -14) * mm});
            skArc(sketch, "E330", {"start": v(43.54, -6.96) * mm, "mid": v(42.83, -9.42) * mm, "end": v(42.41, -11.94) * mm});
            skArc(sketch, "E331", {"start": v(44.63, -3.52) * mm, "mid": v(44.04, -5.22) * mm, "end": v(43.54, -6.96) * mm});
            skArc(sketch, "E332", {"start": v(44.63, -3.52) * mm, "mid": v(44.55, -3.25) * mm, "end": v(44.28, -3.34) * mm});
            skLineSegment(sketch, "E333", {"start": v(57.93, 28.72) * mm, "end": v(56.83, 26.11) * mm});
            skArc(sketch, "E334", {"start": v(57.93, 28.72) * mm, "mid": v(46.7, 24.72) * mm, "end": v(35.6, 20.35) * mm});
            skArc(sketch, "E335", {"start": v(35.6, 20.35) * mm, "mid": v(26.98, 16.96) * mm, "end": v(18.48, 13.28) * mm});
            skArc(sketch, "E336", {"start": v(18.48, 13.28) * mm, "mid": v(17.23, 12.57) * mm, "end": v(16.2, 11.55) * mm});
            skArc(sketch, "E337", {"start": v(16.2, 11.55) * mm, "mid": v(14.91, 9.6) * mm, "end": v(14.34, 7.35) * mm});
            skArc(sketch, "E338", {"start": v(14.91, 5.77) * mm, "mid": v(15.06, 5.63) * mm, "end": v(15.2, 5.5) * mm});
            skPoint(sketch, "E339.visualSharp", {"position": v(14.31, 6.58) * mm});
            skArc(sketch, "E339.filletArc", {"start": v(14.34, 7.35) * mm, "mid": v(14.45, 6.5) * mm, "end": v(14.91, 5.77) * mm});
            skArc(sketch, "E340", {"start": v(15.2, 5.5) * mm, "mid": v(17.03, 4.5) * mm, "end": v(19.1, 4.2) * mm});
            skLineSegment(sketch, "E341", {"start": v(19.1, 4.2) * mm, "end": v(19.1, 6.77) * mm});
            skArc(sketch, "E342", {"start": v(16.63, 7.7) * mm, "mid": v(17.83, 7.15) * mm, "end": v(19.1, 6.77) * mm});
            skArc(sketch, "E343", {"start": v(15.46, 8.39) * mm, "mid": v(16.02, 8) * mm, "end": v(16.63, 7.7) * mm});
            skArc(sketch, "E344", {"start": v(15.46, 8.73) * mm, "mid": v(15.41, 8.56) * mm, "end": v(15.46, 8.39) * mm});
            skArc(sketch, "E345", {"start": v(16.35, 9.41) * mm, "mid": v(15.9, 9.1) * mm, "end": v(15.46, 8.73) * mm});
            skArc(sketch, "E346", {"start": v(20.1, 11.4) * mm, "mid": v(18.18, 10.49) * mm, "end": v(16.35, 9.41) * mm});
            skArc(sketch, "E347", {"start": v(36.04, 17.9) * mm, "mid": v(28.04, 14.73) * mm, "end": v(20.1, 11.4) * mm});
            skArc(sketch, "E348", {"start": v(56.83, 26.11) * mm, "mid": v(46.41, 22.06) * mm, "end": v(36.04, 17.9) * mm});
            skArc(sketch, "E349", {"start": v(29.16, 26.27) * mm, "mid": v(32.73, 27.92) * mm, "end": v(36.2, 29.75) * mm});
            skArc(sketch, "E350", {"start": v(36.2, 29.75) * mm, "mid": v(36.92, 30.2) * mm, "end": v(37.58, 30.73) * mm});
            skArc(sketch, "E351", {"start": v(37.58, 30.73) * mm, "mid": v(37.92, 31.1) * mm, "end": v(38.12, 31.58) * mm});
            skArc(sketch, "E352", {"start": v(38.12, 31.58) * mm, "mid": v(37.8, 32.28) * mm, "end": v(37.08, 32.58) * mm});
            skArc(sketch, "E353", {"start": v(37.08, 32.58) * mm, "mid": v(34, 32.63) * mm, "end": v(30.95, 32.3) * mm});
            skArc(sketch, "E354", {"start": v(30.95, 32.3) * mm, "mid": v(29.68, 32.1) * mm, "end": v(28.42, 31.8) * mm});
            skArc(sketch, "E355", {"start": v(28.77, 33.36) * mm, "mid": v(28.45, 32.61) * mm, "end": v(28.42, 31.8) * mm});
            skArc(sketch, "E356", {"start": v(32.02, 35.75) * mm, "mid": v(30.15, 34.9) * mm, "end": v(28.77, 33.36) * mm});
            skArc(sketch, "E357", {"start": v(39.74, 35.75) * mm, "mid": v(35.88, 36.18) * mm, "end": v(32.02, 35.75) * mm});
            skArc(sketch, "E358", {"start": v(41.74, 34.77) * mm, "mid": v(40.8, 35.38) * mm, "end": v(39.74, 35.75) * mm});
            skArc(sketch, "E359", {"start": v(41.85, 33.8) * mm, "mid": v(41.93, 34.3) * mm, "end": v(41.74, 34.77) * mm});
            skArc(sketch, "E360", {"start": v(37.58, 28.95) * mm, "mid": v(40.03, 31.1) * mm, "end": v(41.85, 33.8) * mm});
            skArc(sketch, "E361", {"start": v(29.3, 25.8) * mm, "mid": v(33.66, 26.8) * mm, "end": v(37.58, 28.95) * mm});
            skArc(sketch, "E362", {"start": v(28.95, 26.18) * mm, "mid": v(29.06, 26.22) * mm, "end": v(29.16, 26.27) * mm});
            skArc(sketch, "E363", {"start": v(29, 25.8) * mm, "mid": v(29.15, 25.78) * mm, "end": v(29.3, 25.8) * mm});
            skArc(sketch, "E364", {"start": v(28.95, 26.18) * mm, "mid": v(28.83, 25.97) * mm, "end": v(29, 25.8) * mm});
            skArc(sketch, "E365", {"start": v(-22, 10.72) * mm, "mid": v(-15.4, 14.76) * mm, "end": v(-8.87, 18.9) * mm});
            skArc(sketch, "E366", {"start": v(-22, 10.72) * mm, "mid": v(-15.2, 13.6) * mm, "end": v(-8.74, 17.16) * mm});
            skArc(sketch, "E367", {"start": v(-4.44, 22.03) * mm, "mid": v(-0.42, 25.1) * mm, "end": v(3.35, 28.49) * mm});
            skArc(sketch, "E368", {"start": v(3.35, 28.49) * mm, "mid": v(6.62, 31.74) * mm, "end": v(9.55, 35.3) * mm});
            skArc(sketch, "E369", {"start": v(9.55, 35.3) * mm, "mid": v(9.94, 35.79) * mm, "end": v(10.29, 36.32) * mm});
            skArc(sketch, "E370", {"start": v(10.29, 36.32) * mm, "mid": v(10.4, 36.61) * mm, "end": v(10.29, 36.9) * mm});
            skArc(sketch, "E371", {"start": v(10.29, 36.9) * mm, "mid": v(9.49, 37.57) * mm, "end": v(8.63, 38.17) * mm});
            skArc(sketch, "E372", {"start": v(6.72, 39.83) * mm, "mid": v(7.63, 38.94) * mm, "end": v(8.63, 38.17) * mm});
            skArc(sketch, "E373", {"start": v(6, 41.61) * mm, "mid": v(6.18, 40.65) * mm, "end": v(6.72, 39.83) * mm});
            skArc(sketch, "E374", {"start": v(6.46, 43.33) * mm, "mid": v(6.14, 42.5) * mm, "end": v(6, 41.61) * mm});
            skArc(sketch, "E375", {"start": v(8.88, 46.75) * mm, "mid": v(7.5, 45.16) * mm, "end": v(6.46, 43.33) * mm});
            skArc(sketch, "E376", {"start": v(10.6, 46.75) * mm, "mid": v(9.74, 47) * mm, "end": v(8.88, 46.75) * mm});
            skArc(sketch, "E377", {"start": v(12.14, 44.92) * mm, "mid": v(11.5, 45.94) * mm, "end": v(10.6, 46.75) * mm});
            skArc(sketch, "E378", {"start": v(12.29, 38.7) * mm, "mid": v(12.92, 41.83) * mm, "end": v(12.14, 44.92) * mm});
            skArc(sketch, "E379", {"start": v(12.29, 38.7) * mm, "mid": v(12.17, 38.35) * mm, "end": v(12.2, 37.98) * mm});
            skArc(sketch, "E380", {"start": v(13.43, 35.97) * mm, "mid": v(12.97, 37.07) * mm, "end": v(12.2, 37.98) * mm});
            skArc(sketch, "E381", {"start": v(13.7, 34) * mm, "mid": v(13.63, 34.99) * mm, "end": v(13.43, 35.97) * mm});
            skPoint(sketch, "E382.orphan", {"position": v(13.43, 32.02) * mm});
            skArc(sketch, "E383", {"start": v(12.95, 29.56) * mm, "mid": v(13.5, 31.74) * mm, "end": v(13.7, 34) * mm});
            skArc(sketch, "E384", {"start": v(11.42, 24.45) * mm, "mid": v(12.2, 27) * mm, "end": v(12.95, 29.56) * mm});
            skArc(sketch, "E385", {"start": v(11.42, 24.45) * mm, "mid": v(11.16, 22.95) * mm, "end": v(11.09, 21.44) * mm});
            skArc(sketch, "E386", {"start": v(11.09, 21.44) * mm, "mid": v(11.31, 20.7) * mm, "end": v(12, 20.32) * mm});
            skArc(sketch, "E387", {"start": v(12, 20.32) * mm, "mid": v(13.04, 20.31) * mm, "end": v(14, 20.76) * mm});
            skArc(sketch, "E388", {"start": v(14, 20.76) * mm, "mid": v(14.86, 21.66) * mm, "end": v(15.62, 22.66) * mm});
            skArc(sketch, "E389", {"start": v(16.52, 23.45) * mm, "mid": v(16.02, 23.1) * mm, "end": v(15.62, 22.66) * mm});
            skArc(sketch, "E390", {"start": v(17.45, 23.55) * mm, "mid": v(16.98, 23.58) * mm, "end": v(16.52, 23.45) * mm});
            skArc(sketch, "E391", {"start": v(17.58, 23.25) * mm, "mid": v(17.58, 23.43) * mm, "end": v(17.45, 23.55) * mm});
            skArc(sketch, "E392", {"start": v(17.54, 23.2) * mm, "mid": v(17.18, 22.95) * mm, "end": v(16.84, 22.66) * mm});
            skPoint(sketch, "E393.visualSharp", {"position": v(17.56, 23.22) * mm});
            skArc(sketch, "E393.filletArc", {"start": v(17.54, 23.2) * mm, "mid": v(17.56, 23.23) * mm, "end": v(17.58, 23.25) * mm});
            skArc(sketch, "E394", {"start": v(16.84, 22.66) * mm, "mid": v(15.8, 21.49) * mm, "end": v(14.85, 20.23) * mm});
            skArc(sketch, "E395", {"start": v(12.75, 18.43) * mm, "mid": v(13.93, 19.17) * mm, "end": v(14.85, 20.23) * mm});
            skArc(sketch, "E396", {"start": v(10.23, 19.18) * mm, "mid": v(11.38, 18.42) * mm, "end": v(12.75, 18.43) * mm});
            skArc(sketch, "E397", {"start": v(9.85, 20.46) * mm, "mid": v(9.95, 19.8) * mm, "end": v(10.23, 19.18) * mm});
            skArc(sketch, "E398", {"start": v(10.74, 24.16) * mm, "mid": v(10.07, 22.36) * mm, "end": v(9.85, 20.46) * mm});
            skArc(sketch, "E399", {"start": v(10.83, 24.37) * mm, "mid": v(11.4, 26.04) * mm, "end": v(11.9, 27.74) * mm});
            skPoint(sketch, "E400.visualSharp", {"position": v(10.79, 24.25) * mm});
            skArc(sketch, "E400.filletArc", {"start": v(10.74, 24.16) * mm, "mid": v(10.79, 24.26) * mm, "end": v(10.83, 24.37) * mm});
            skArc(sketch, "E401", {"start": v(11.9, 27.74) * mm, "mid": v(12.13, 28.64) * mm, "end": v(12.25, 29.56) * mm});
            skArc(sketch, "E402", {"start": v(12.25, 29.56) * mm, "mid": v(12.34, 31.48) * mm, "end": v(12.25, 33.4) * mm});
            skArc(sketch, "E403", {"start": v(12.25, 33.4) * mm, "mid": v(11.89, 34.78) * mm, "end": v(11.15, 36) * mm});
            skArc(sketch, "E404", {"start": v(5.83, 29.08) * mm, "mid": v(8.65, 32.42) * mm, "end": v(11.15, 36) * mm});
            skArc(sketch, "E405", {"start": v(-4.31, 20.23) * mm, "mid": v(0.98, 24.4) * mm, "end": v(5.83, 29.08) * mm});
            skArc(sketch, "E406", {"start": v(7.97, 42.4) * mm, "mid": v(9.47, 40.94) * mm, "end": v(11.08, 39.6) * mm});
            skArc(sketch, "E407", {"start": v(11.08, 39.6) * mm, "mid": v(11.14, 39.55) * mm, "end": v(11.2, 39.5) * mm});
            skArc(sketch, "E408", {"start": v(11.34, 39.6) * mm, "mid": v(11.34, 39.63) * mm, "end": v(11.34, 39.66) * mm});
            skArc(sketch, "E409", {"start": v(11.34, 39.66) * mm, "mid": v(11.26, 40.57) * mm, "end": v(11.08, 41.47) * mm});
            skPoint(sketch, "E410.visualSharp", {"position": v(11.34, 39.44) * mm});
            skArc(sketch, "E410.filletArc", {"start": v(11.2, 39.5) * mm, "mid": v(11.3, 39.5) * mm, "end": v(11.34, 39.6) * mm});
            skArc(sketch, "E411", {"start": v(11.08, 41.47) * mm, "mid": v(10.53, 42.75) * mm, "end": v(9.72, 43.88) * mm});
            skArc(sketch, "E412", {"start": v(9.72, 43.88) * mm, "mid": v(9.53, 44.08) * mm, "end": v(9.34, 44.28) * mm});
            skArc(sketch, "E413", {"start": v(9.34, 44.28) * mm, "mid": v(8.94, 44.5) * mm, "end": v(8.5, 44.43) * mm});
            skArc(sketch, "E414", {"start": v(8.5, 44.43) * mm, "mid": v(7.99, 44) * mm, "end": v(7.65, 43.41) * mm});
            skArc(sketch, "E415", {"start": v(7.65, 43.41) * mm, "mid": v(7.66, 42.86) * mm, "end": v(7.97, 42.4) * mm});
            skArc(sketch, "E416", {"start": v(-25.72, 33.06) * mm, "mid": v(-24.9, 34.53) * mm, "end": v(-24.37, 36.12) * mm});
            skArc(sketch, "E417", {"start": v(-24.37, 36.12) * mm, "mid": v(-24.1, 37.3) * mm, "end": v(-23.93, 38.5) * mm});
            skArc(sketch, "E418", {"start": v(-23.15, 41.54) * mm, "mid": v(-23.61, 40.04) * mm, "end": v(-23.93, 38.5) * mm});
            skArc(sketch, "E419", {"start": v(-21.75, 44.83) * mm, "mid": v(-22.55, 43.23) * mm, "end": v(-23.15, 41.54) * mm});
            skArc(sketch, "E420", {"start": v(-20.26, 45.2) * mm, "mid": v(-21.1, 45.38) * mm, "end": v(-21.75, 44.83) * mm});
            skArc(sketch, "E421", {"start": v(-18.5, 43.76) * mm, "mid": v(-19.35, 44.52) * mm, "end": v(-20.26, 45.2) * mm});
            skArc(sketch, "E422", {"start": v(-18.5, 43.76) * mm, "mid": v(-18.33, 43.66) * mm, "end": v(-18.13, 43.62) * mm});
            skArc(sketch, "E423", {"start": v(-18.13, 43.62) * mm, "mid": v(-18.04, 43.7) * mm, "end": v(-17.96, 43.79) * mm});
            skPoint(sketch, "E424.orphan", {"position": v(-17.44, 45.2) * mm});
            skArc(sketch, "E425", {"start": v(-17.96, 43.79) * mm, "mid": v(-17.55, 44.36) * mm, "end": v(-17.35, 45.03) * mm});
            skArc(sketch, "E426", {"start": v(-17.35, 45.03) * mm, "mid": v(-17.27, 45.7) * mm, "end": v(-17.26, 46.37) * mm});
            skArc(sketch, "E427", {"start": v(-17.26, 46.37) * mm, "mid": v(-17.3, 46.56) * mm, "end": v(-17.37, 46.73) * mm});
            skArc(sketch, "E428", {"start": v(-17.37, 46.73) * mm, "mid": v(-18.02, 47.76) * mm, "end": v(-18.91, 48.58) * mm});
            skArc(sketch, "E429", {"start": v(-18.91, 48.58) * mm, "mid": v(-20.06, 48.93) * mm, "end": v(-21.21, 48.58) * mm});
            skArc(sketch, "E430", {"start": v(-21.21, 48.58) * mm, "mid": v(-21.96, 48) * mm, "end": v(-22.53, 47.25) * mm});
            skArc(sketch, "E431", {"start": v(-22.7, 46.96) * mm, "mid": v(-23.73, 45.05) * mm, "end": v(-24.36, 42.99) * mm});
            skPoint(sketch, "E432.visualSharp", {"position": v(-22.6, 47.12) * mm});
            skArc(sketch, "E432.filletArc", {"start": v(-22.7, 46.96) * mm, "mid": v(-22.62, 47.1) * mm, "end": v(-22.53, 47.25) * mm});
            skArc(sketch, "E433", {"start": v(-24.36, 42.99) * mm, "mid": v(-24.9, 40.87) * mm, "end": v(-25.36, 38.74) * mm});
            skArc(sketch, "E434", {"start": v(-25.36, 38.74) * mm, "mid": v(-25.4, 38.46) * mm, "end": v(-25.45, 38.18) * mm});
            skArc(sketch, "E435", {"start": v(-25.56, 37.91) * mm, "mid": v(-25.53, 37.96) * mm, "end": v(-25.5, 38) * mm});
            skArc(sketch, "E436", {"start": v(-25.76, 37.98) * mm, "mid": v(-25.67, 37.9) * mm, "end": v(-25.56, 37.91) * mm});
            skPoint(sketch, "E437.visualSharp", {"position": v(-25.45, 38.12) * mm});
            skArc(sketch, "E437.filletArc", {"start": v(-25.5, 38) * mm, "mid": v(-25.47, 38.09) * mm, "end": v(-25.45, 38.18) * mm});
            skArc(sketch, "E438", {"start": v(-25.8, 38.1) * mm, "mid": v(-25.78, 38.04) * mm, "end": v(-25.76, 37.98) * mm});
            skArc(sketch, "E439", {"start": v(-25.88, 38.62) * mm, "mid": v(-25.85, 38.36) * mm, "end": v(-25.8, 38.1) * mm});
            skArc(sketch, "E440", {"start": v(-25.88, 38.62) * mm, "mid": v(-25.99, 39.14) * mm, "end": v(-26.14, 39.64) * mm});
            skArc(sketch, "E441", {"start": v(-26.14, 39.64) * mm, "mid": v(-26.8, 41.67) * mm, "end": v(-27.67, 43.62) * mm});
            skArc(sketch, "E442", {"start": v(-27.67, 43.62) * mm, "mid": v(-28.93, 45.6) * mm, "end": v(-30.82, 46.98) * mm});
            skArc(sketch, "E443", {"start": v(-30.82, 46.98) * mm, "mid": v(-31.83, 47.31) * mm, "end": v(-32.9, 47.19) * mm});
            skArc(sketch, "E444", {"start": v(-32.9, 47.19) * mm, "mid": v(-34.02, 46.25) * mm, "end": v(-34.72, 44.97) * mm});
            skArc(sketch, "E445", {"start": v(-34.72, 44.97) * mm, "mid": v(-34.87, 44.56) * mm, "end": v(-34.97, 44.14) * mm});
            skArc(sketch, "E446", {"start": v(-34.9, 43.55) * mm, "mid": v(-34.74, 43.29) * mm, "end": v(-34.52, 43.06) * mm});
            skPoint(sketch, "E447.visualSharp", {"position": v(-35, 43.9) * mm});
            skArc(sketch, "E447.filletArc", {"start": v(-34.97, 44.14) * mm, "mid": v(-34.98, 43.84) * mm, "end": v(-34.9, 43.55) * mm});
            skArc(sketch, "E448", {"start": v(-34.52, 43.06) * mm, "mid": v(-33.81, 42.4) * mm, "end": v(-33.02, 41.83) * mm});
            skArc(sketch, "E449", {"start": v(-33.02, 41.83) * mm, "mid": v(-32.58, 41.64) * mm, "end": v(-32.1, 41.63) * mm});
            skArc(sketch, "E450", {"start": v(-32.1, 41.63) * mm, "mid": v(-31.7, 41.71) * mm, "end": v(-31.31, 41.87) * mm});
            skArc(sketch, "E451", {"start": v(-30.68, 42.07) * mm, "mid": v(-31.02, 42.04) * mm, "end": v(-31.31, 41.87) * mm});
            skArc(sketch, "E452", {"start": v(-30.11, 41.62) * mm, "mid": v(-30.36, 41.9) * mm, "end": v(-30.68, 42.07) * mm});
            skArc(sketch, "E453", {"start": v(-28.54, 39.05) * mm, "mid": v(-29.25, 40.38) * mm, "end": v(-30.11, 41.62) * mm});
            skArc(sketch, "E454", {"start": v(-27.05, 35.2) * mm, "mid": v(-27.67, 37.17) * mm, "end": v(-28.54, 39.05) * mm});
            skArc(sketch, "E455", {"start": v(-26.64, 33.05) * mm, "mid": v(-26.83, 34.13) * mm, "end": v(-27.05, 35.2) * mm});
            skArc(sketch, "E456", {"start": v(-26.08, 32.63) * mm, "mid": v(-25.88, 32.82) * mm, "end": v(-25.72, 33.06) * mm});
            skArc(sketch, "E457", {"start": v(-26.33, 32.63) * mm, "mid": v(-26.2, 32.6) * mm, "end": v(-26.08, 32.63) * mm});
            skArc(sketch, "E458", {"start": v(-26.57, 32.85) * mm, "mid": v(-26.46, 32.73) * mm, "end": v(-26.33, 32.63) * mm});
            skPoint(sketch, "E459.visualSharp", {"position": v(-26.63, 32.98) * mm});
            skArc(sketch, "E459.filletArc", {"start": v(-26.64, 33.05) * mm, "mid": v(-26.62, 32.95) * mm, "end": v(-26.57, 32.85) * mm});
            skArc(sketch, "E460", {"start": v(-52.89, -2.83) * mm, "mid": v(-54.35, -5.9) * mm, "end": v(-55.43, -9.12) * mm});
            skArc(sketch, "E461", {"start": v(-55.43, -9.12) * mm, "mid": v(-56.12, -12.11) * mm, "end": v(-56.14, -15.18) * mm});
            skArc(sketch, "E462", {"start": v(-56.14, -15.18) * mm, "mid": v(-55.66, -16.55) * mm, "end": v(-54.62, -17.57) * mm});
            skArc(sketch, "E463", {"start": v(-54.62, -17.57) * mm, "mid": v(-53.87, -17.72) * mm, "end": v(-53.12, -17.57) * mm});
            skArc(sketch, "E464", {"start": v(-53.12, -17.57) * mm, "mid": v(-52.43, -16.95) * mm, "end": v(-51.92, -16.18) * mm});
            skArc(sketch, "E465", {"start": v(-51.92, -16.18) * mm, "mid": v(-51.38, -14.97) * mm, "end": v(-51.04, -13.7) * mm});
            skArc(sketch, "E466", {"start": v(-51.04, -13.7) * mm, "mid": v(-50.93, -13.13) * mm, "end": v(-50.84, -12.56) * mm});
            skArc(sketch, "E467", {"start": v(-50.84, -12.56) * mm, "mid": v(-50.82, -12.31) * mm, "end": v(-50.83, -12.06) * mm});
            skArc(sketch, "E468", {"start": v(-50.9, -11.98) * mm, "mid": v(-51.05, -12) * mm, "end": v(-51.13, -12.14) * mm});
            skPoint(sketch, "E469.visualSharp", {"position": v(-50.84, -12.02) * mm});
            skArc(sketch, "E469.filletArc", {"start": v(-50.83, -12.06) * mm, "mid": v(-50.85, -12.02) * mm, "end": v(-50.9, -11.98) * mm});
            skPoint(sketch, "E470.visualSharp", {"position": v(-51.13, -12.14) * mm});
            skArc(sketch, "E470.filletArc", {"start": v(-51.14, -12.16) * mm, "mid": v(-51.13, -12.15) * mm, "end": v(-51.13, -12.14) * mm});
            skArc(sketch, "E471", {"start": v(-52.6, -14.23) * mm, "mid": v(-51.9, -13.59) * mm, "end": v(-51.4, -12.8) * mm});
            skPoint(sketch, "E472.visualSharp", {"position": v(-51.34, -12.68) * mm});
            skArc(sketch, "E472.filletArc", {"start": v(-51.29, -12.6) * mm, "mid": v(-51.34, -12.7) * mm, "end": v(-51.4, -12.8) * mm});
            skArc(sketch, "E473", {"start": v(-51.29, -12.6) * mm, "mid": v(-51.2, -12.39) * mm, "end": v(-51.14, -12.16) * mm});
            skArc(sketch, "E474", {"start": v(-53.7, -14.43) * mm, "mid": v(-53.12, -14.45) * mm, "end": v(-52.6, -14.23) * mm});
            skArc(sketch, "E475", {"start": v(-54.6, -13.49) * mm, "mid": v(-54.28, -14.08) * mm, "end": v(-53.7, -14.43) * mm});
            skArc(sketch, "E476", {"start": v(-54.76, -11.44) * mm, "mid": v(-54.78, -12.47) * mm, "end": v(-54.6, -13.49) * mm});
            skArc(sketch, "E477", {"start": v(-53.63, -6.45) * mm, "mid": v(-54.34, -8.91) * mm, "end": v(-54.76, -11.44) * mm});
            skArc(sketch, "E478", {"start": v(-52.54, -3.02) * mm, "mid": v(-53.13, -4.72) * mm, "end": v(-53.63, -6.45) * mm});
            skArc(sketch, "E479", {"start": v(-52.54, -3.02) * mm, "mid": v(-52.62, -2.75) * mm, "end": v(-52.89, -2.83) * mm});
            skArc(sketch, "E480", {"start": v(-40.4, 27.48) * mm, "mid": v(-40.37, 26.84) * mm, "end": v(-40.25, 26.21) * mm});
            skArc(sketch, "E481", {"start": v(-40.25, 26.21) * mm, "mid": v(-39.93, 25.23) * mm, "end": v(-39.46, 24.3) * mm});
            skArc(sketch, "E482", {"start": v(-38.54, 21.88) * mm, "mid": v(-38.88, 23.14) * mm, "end": v(-39.46, 24.3) * mm});
            skArc(sketch, "E483", {"start": v(-39.46, 17.35) * mm, "mid": v(-38.6, 19.53) * mm, "end": v(-38.54, 21.88) * mm});
            skArc(sketch, "E484", {"start": v(-40.7, 16.3) * mm, "mid": v(-40, 16.74) * mm, "end": v(-39.46, 17.35) * mm});
            skArc(sketch, "E485", {"start": v(-41.97, 16.3) * mm, "mid": v(-41.33, 16.23) * mm, "end": v(-40.7, 16.3) * mm});
            skArc(sketch, "E486", {"start": v(-44.08, 19.03) * mm, "mid": v(-43.93, 18.27) * mm, "end": v(-43.56, 17.6) * mm});
            skArc(sketch, "E487", {"start": v(-43.56, 17.6) * mm, "mid": v(-43.2, 17.08) * mm, "end": v(-42.73, 16.65) * mm});
            skArc(sketch, "E488", {"start": v(-42.73, 16.65) * mm, "mid": v(-42.37, 16.45) * mm, "end": v(-41.97, 16.3) * mm});
            skArc(sketch, "E489", {"start": v(-44.77, 17.3) * mm, "mid": v(-44.34, 18.13) * mm, "end": v(-44.08, 19.03) * mm});
            skArc(sketch, "E490", {"start": v(-46.22, 15.9) * mm, "mid": v(-45.43, 16.53) * mm, "end": v(-44.77, 17.3) * mm});
            skArc(sketch, "E491", {"start": v(-47.83, 15.56) * mm, "mid": v(-47, 15.6) * mm, "end": v(-46.22, 15.9) * mm});
            skArc(sketch, "E492", {"start": v(-49.27, 16.23) * mm, "mid": v(-48.61, 15.76) * mm, "end": v(-47.83, 15.56) * mm});
            skArc(sketch, "E493", {"start": v(-49.96, 17.67) * mm, "mid": v(-49.7, 16.9) * mm, "end": v(-49.27, 16.23) * mm});
            skArc(sketch, "E494", {"start": v(-50.08, 18.35) * mm, "mid": v(-50.04, 18) * mm, "end": v(-49.96, 17.67) * mm});
            skArc(sketch, "E495", {"start": v(-50.08, 19.02) * mm, "mid": v(-50.09, 18.68) * mm, "end": v(-50.08, 18.35) * mm});
            skArc(sketch, "E496", {"start": v(-50.08, 20.86) * mm, "mid": v(-50.1, 19.94) * mm, "end": v(-50.08, 19.02) * mm});
            skArc(sketch, "E497", {"start": v(-50.08, 22.3) * mm, "mid": v(-50.1, 21.58) * mm, "end": v(-50.08, 20.86) * mm});
            skArc(sketch, "E498", {"start": v(-50.08, 22.3) * mm, "mid": v(-50.24, 22.78) * mm, "end": v(-50.66, 23.05) * mm});
            skArc(sketch, "E499", {"start": v(-50.94, 23.2) * mm, "mid": v(-50.81, 23.1) * mm, "end": v(-50.66, 23.05) * mm});
            skArc(sketch, "E500", {"start": v(-50.77, 24.64) * mm, "mid": v(-50.98, 23.94) * mm, "end": v(-50.94, 23.2) * mm});
            skArc(sketch, "E501", {"start": v(-49.45, 26.32) * mm, "mid": v(-50.22, 25.56) * mm, "end": v(-50.77, 24.64) * mm});
            skArc(sketch, "E502", {"start": v(-49.2, 26.31) * mm, "mid": v(-49.3, 26.35) * mm, "end": v(-49.41, 26.34) * mm});
            skPoint(sketch, "E503.visualSharp", {"position": v(-49.43, 26.34) * mm});
            skArc(sketch, "E503.filletArc", {"start": v(-49.41, 26.34) * mm, "mid": v(-49.43, 26.34) * mm, "end": v(-49.45, 26.32) * mm});
            skArc(sketch, "E504", {"start": v(-48.97, 25.99) * mm, "mid": v(-49.04, 26.19) * mm, "end": v(-49.2, 26.31) * mm});
            skArc(sketch, "E505", {"start": v(-48.97, 25.99) * mm, "mid": v(-49.01, 24.2) * mm, "end": v(-48.97, 22.4) * mm});
            skArc(sketch, "E506", {"start": v(-48.97, 22.4) * mm, "mid": v(-48.94, 21.4) * mm, "end": v(-48.79, 20.4) * mm});
            skArc(sketch, "E507", {"start": v(-48.79, 20.4) * mm, "mid": v(-48.41, 19.43) * mm, "end": v(-47.7, 18.67) * mm});
            skArc(sketch, "E508", {"start": v(-47.7, 18.67) * mm, "mid": v(-46.8, 18.54) * mm, "end": v(-45.96, 18.89) * mm});
            skArc(sketch, "E509", {"start": v(-45.96, 18.89) * mm, "mid": v(-45.2, 19.55) * mm, "end": v(-44.66, 20.4) * mm});
            skArc(sketch, "E510", {"start": v(-44.66, 20.4) * mm, "mid": v(-44.54, 21.4) * mm, "end": v(-44.66, 22.4) * mm});
            skArc(sketch, "E511", {"start": v(-44.66, 22.4) * mm, "mid": v(-45.01, 23.98) * mm, "end": v(-45.54, 25.5) * mm});
            skArc(sketch, "E512", {"start": v(-45.54, 26.2) * mm, "mid": v(-45.6, 25.86) * mm, "end": v(-45.54, 25.5) * mm});
            skArc(sketch, "E513", {"start": v(-44.8, 27.44) * mm, "mid": v(-45.22, 26.85) * mm, "end": v(-45.54, 26.2) * mm});
            skArc(sketch, "E514", {"start": v(-44.66, 27.56) * mm, "mid": v(-44.74, 27.5) * mm, "end": v(-44.8, 27.44) * mm});
            skArc(sketch, "E515", {"start": v(-44.55, 27.56) * mm, "mid": v(-44.6, 27.57) * mm, "end": v(-44.66, 27.56) * mm});
            skArc(sketch, "E516", {"start": v(-44.3, 27.3) * mm, "mid": v(-44.4, 27.44) * mm, "end": v(-44.55, 27.56) * mm});
            skArc(sketch, "E517", {"start": v(-43.31, 23.47) * mm, "mid": v(-43.6, 25.43) * mm, "end": v(-44.3, 27.3) * mm});
            skArc(sketch, "E518", {"start": v(-43.31, 23.47) * mm, "mid": v(-43.23, 22.38) * mm, "end": v(-43.13, 21.28) * mm});
            skArc(sketch, "E519", {"start": v(-43.13, 21.28) * mm, "mid": v(-42.97, 20.52) * mm, "end": v(-42.6, 19.83) * mm});
            skArc(sketch, "E520", {"start": v(-42.6, 19.83) * mm, "mid": v(-41.97, 19.3) * mm, "end": v(-41.14, 19.18) * mm});
            skArc(sketch, "E521", {"start": v(-41.14, 19.18) * mm, "mid": v(-40.46, 19.4) * mm, "end": v(-39.9, 19.83) * mm});
            skArc(sketch, "E522", {"start": v(-39.9, 19.83) * mm, "mid": v(-39.83, 20) * mm, "end": v(-39.78, 20.18) * mm});
            skArc(sketch, "E523", {"start": v(-39.78, 20.18) * mm, "mid": v(-39.82, 20.37) * mm, "end": v(-39.88, 20.55) * mm});
            skArc(sketch, "E524", {"start": v(-40.63, 22) * mm, "mid": v(-40.29, 21.25) * mm, "end": v(-39.88, 20.55) * mm});
            skArc(sketch, "E525", {"start": v(-41.36, 23.83) * mm, "mid": v(-41.04, 22.9) * mm, "end": v(-40.63, 22) * mm});
            skArc(sketch, "E526", {"start": v(-41.77, 25.35) * mm, "mid": v(-41.61, 24.58) * mm, "end": v(-41.36, 23.83) * mm});
            skArc(sketch, "E527", {"start": v(-41.54, 26.97) * mm, "mid": v(-41.77, 26.17) * mm, "end": v(-41.77, 25.35) * mm});
            skArc(sketch, "E528", {"start": v(-40.62, 28.35) * mm, "mid": v(-41.14, 27.7) * mm, "end": v(-41.54, 26.97) * mm});
            skArc(sketch, "E529", {"start": v(-40.4, 27.74) * mm, "mid": v(-40.4, 27.6) * mm, "end": v(-40.4, 27.48) * mm});
            skArc(sketch, "E530", {"start": v(-40.4, 27.74) * mm, "mid": v(-40.4, 27.88) * mm, "end": v(-40.4, 28.02) * mm});
            skArc(sketch, "E531", {"start": v(-40.4, 28.02) * mm, "mid": v(-40.44, 28.12) * mm, "end": v(-40.5, 28.21) * mm});
            skArc(sketch, "E532", {"start": v(-40.5, 28.21) * mm, "mid": v(-40.56, 28.29) * mm, "end": v(-40.62, 28.35) * mm});
            skLineSegment(sketch, "E533", {"start": v(-46.63, 46.36) * mm, "end": v(-48.1, 43.7) * mm});
            skArc(sketch, "E534", {"start": v(-43.76, 39.14) * mm, "mid": v(-44.67, 42.96) * mm, "end": v(-46.63, 46.36) * mm});
            skArc(sketch, "E535", {"start": v(-45.17, 28.63) * mm, "mid": v(-43.7, 33.79) * mm, "end": v(-43.76, 39.14) * mm});
            skArc(sketch, "E536", {"start": v(-45.42, 37.96) * mm, "mid": v(-46.6, 40.9) * mm, "end": v(-48.1, 43.7) * mm});
            skArc(sketch, "E537", {"start": v(-45.58, 28.95) * mm, "mid": v(-44.92, 32.41) * mm, "end": v(-44.97, 35.93) * mm});
            skPoint(sketch, "E538.visualSharp", {"position": v(-45.14, 37.06) * mm});
            skArc(sketch, "E538.filletArc", {"start": v(-44.97, 35.93) * mm, "mid": v(-45.14, 36.95) * mm, "end": v(-45.42, 37.96) * mm});
            skArc(sketch, "E539", {"start": v(-45.58, 28.95) * mm, "mid": v(-45.59, 28.7) * mm, "end": v(-45.58, 28.46) * mm});
            skArc(sketch, "E540", {"start": v(-45.34, 28.33) * mm, "mid": v(-45.25, 28.48) * mm, "end": v(-45.17, 28.63) * mm});
            skArc(sketch, "E541", {"start": v(-45.45, 28.28) * mm, "mid": v(-45.39, 28.3) * mm, "end": v(-45.34, 28.33) * mm});
            skArc(sketch, "E542", {"start": v(-45.58, 28.46) * mm, "mid": v(-45.54, 28.35) * mm, "end": v(-45.45, 28.28) * mm});
            skArc(sketch, "E543", {"start": v(-62.82, 24.9) * mm, "mid": v(-65.35, 28.16) * mm, "end": v(-68.87, 30.32) * mm});
            skArc(sketch, "E544", {"start": v(-62.67, 22.9) * mm, "mid": v(-62.55, 23.92) * mm, "end": v(-62.82, 24.9) * mm});
            skArc(sketch, "E545", {"start": v(-64.07, 20.4) * mm, "mid": v(-63.22, 21.56) * mm, "end": v(-62.67, 22.9) * mm});
            skArc(sketch, "E546", {"start": v(-64.54, 20.22) * mm, "mid": v(-64.29, 20.26) * mm, "end": v(-64.07, 20.4) * mm});
            skArc(sketch, "E547", {"start": v(-68.4, 20.9) * mm, "mid": v(-66.5, 20.43) * mm, "end": v(-64.54, 20.22) * mm});
            skArc(sketch, "E548", {"start": v(-68.87, 30.32) * mm, "mid": v(-70.07, 30.5) * mm, "end": v(-71.21, 30.12) * mm});
            skArc(sketch, "E549", {"start": v(-71.21, 30.12) * mm, "mid": v(-71.66, 29.67) * mm, "end": v(-71.94, 29.1) * mm});
            skArc(sketch, "E550", {"start": v(-71.94, 29.1) * mm, "mid": v(-72.06, 28.13) * mm, "end": v(-71.94, 27.17) * mm});
            skArc(sketch, "E551", {"start": v(-71.88, 26.6) * mm, "mid": v(-71.86, 26.89) * mm, "end": v(-71.94, 27.17) * mm});
            skArc(sketch, "E552", {"start": v(-71.88, 26.6) * mm, "mid": v(-72.65, 24.93) * mm, "end": v(-72.74, 23.1) * mm});
            skArc(sketch, "E553", {"start": v(-72.74, 23.1) * mm, "mid": v(-72.19, 22.13) * mm, "end": v(-71.21, 21.58) * mm});
            skArc(sketch, "E554", {"start": v(-69.5, 21.02) * mm, "mid": v(-70.36, 21.3) * mm, "end": v(-71.21, 21.58) * mm});
            skArc(sketch, "E555", {"start": v(-71.5, 16.68) * mm, "mid": v(-69.7, 18.6) * mm, "end": v(-68.4, 20.9) * mm});
            skArc(sketch, "E556", {"start": v(-75.83, 14.1) * mm, "mid": v(-73.6, 15.28) * mm, "end": v(-71.5, 16.68) * mm});
            skArc(sketch, "E557", {"start": v(-75.83, 14.1) * mm, "mid": v(-76.13, 13.93) * mm, "end": v(-76.38, 13.69) * mm});
            skArc(sketch, "E558", {"start": v(-76.34, 13.02) * mm, "mid": v(-76.04, 12.8) * mm, "end": v(-75.69, 12.7) * mm});
            skArc(sketch, "E559", {"start": v(-75.69, 12.7) * mm, "mid": v(-71.63, 12.67) * mm, "end": v(-67.63, 13.35) * mm});
            skArc(sketch, "E560", {"start": v(-67.63, 13.35) * mm, "mid": v(-65.35, 13.8) * mm, "end": v(-63.1, 14.39) * mm});
            skArc(sketch, "E561", {"start": v(-67.2, 11.8) * mm, "mid": v(-65.03, 12.9) * mm, "end": v(-63.1, 14.39) * mm});
            skArc(sketch, "E562", {"start": v(-72.14, 10.4) * mm, "mid": v(-69.64, 10.96) * mm, "end": v(-67.2, 11.8) * mm});
            skArc(sketch, "E563", {"start": v(-76.33, 10.4) * mm, "mid": v(-74.24, 10.23) * mm, "end": v(-72.14, 10.4) * mm});
            skArc(sketch, "E564", {"start": v(-77.47, 11.41) * mm, "mid": v(-77, 10.78) * mm, "end": v(-76.33, 10.4) * mm});
            skArc(sketch, "E565", {"start": v(-77.6, 13.01) * mm, "mid": v(-77.63, 12.2) * mm, "end": v(-77.47, 11.41) * mm});
            skArc(sketch, "E566", {"start": v(-76.15, 15.5) * mm, "mid": v(-77.12, 14.4) * mm, "end": v(-77.6, 13.01) * mm});
            skPoint(sketch, "E567.visualSharp", {"position": v(-76.58, 13.35) * mm});
            skArc(sketch, "E567.filletArc", {"start": v(-76.38, 13.69) * mm, "mid": v(-76.49, 13.35) * mm, "end": v(-76.34, 13.02) * mm});
            skArc(sketch, "E568", {"start": v(-72.26, 18.23) * mm, "mid": v(-70.76, 19.5) * mm, "end": v(-69.5, 21.02) * mm});
            skArc(sketch, "E569", {"start": v(-72.26, 18.23) * mm, "mid": v(-73.53, 17.44) * mm, "end": v(-74.73, 16.55) * mm});
            skArc(sketch, "E570", {"start": v(-67.47, 23.22) * mm, "mid": v(-67.27, 24.53) * mm, "end": v(-67.27, 25.86) * mm});
            skArc(sketch, "E571", {"start": v(-64.03, 22.63) * mm, "mid": v(-65.63, 22.84) * mm, "end": v(-67.25, 22.94) * mm});
            skArc(sketch, "E572", {"start": v(-64.03, 22.63) * mm, "mid": v(-64, 22.88) * mm, "end": v(-64.03, 23.12) * mm});
            skArc(sketch, "E573", {"start": v(-64.03, 23.12) * mm, "mid": v(-64.63, 24.23) * mm, "end": v(-65.53, 25.12) * mm});
            skArc(sketch, "E574", {"start": v(-65.8, 25.33) * mm, "mid": v(-66.24, 25.64) * mm, "end": v(-66.7, 25.9) * mm});
            skPoint(sketch, "E575.visualSharp", {"position": v(-65.66, 25.21) * mm});
            skArc(sketch, "E575.filletArc", {"start": v(-65.8, 25.33) * mm, "mid": v(-65.66, 25.22) * mm, "end": v(-65.53, 25.12) * mm});
            skArc(sketch, "E576", {"start": v(-66.7, 25.9) * mm, "mid": v(-66.87, 25.96) * mm, "end": v(-67.03, 26.02) * mm});
            skArc(sketch, "E577", {"start": v(-67.03, 26.02) * mm, "mid": v(-67.2, 26) * mm, "end": v(-67.27, 25.86) * mm});
            skArc(sketch, "E578", {"start": v(-67.47, 23.22) * mm, "mid": v(-67.41, 23.03) * mm, "end": v(-67.25, 22.94) * mm});
            skArc(sketch, "E579", {"start": v(-70.16, 26.55) * mm, "mid": v(-70.97, 25.79) * mm, "end": v(-71.65, 24.9) * mm});
            skArc(sketch, "E580", {"start": v(-69.27, 26.55) * mm, "mid": v(-69.72, 26.63) * mm, "end": v(-70.16, 26.55) * mm});
            skArc(sketch, "E581", {"start": v(-68.77, 26) * mm, "mid": v(-68.97, 26.31) * mm, "end": v(-69.27, 26.55) * mm});
            skArc(sketch, "E582", {"start": v(-68.66, 23.33) * mm, "mid": v(-68.6, 24.67) * mm, "end": v(-68.77, 26) * mm});
            skArc(sketch, "E583", {"start": v(-71.65, 24.9) * mm, "mid": v(-71.72, 24.68) * mm, "end": v(-71.65, 24.46) * mm});
            skArc(sketch, "E584", {"start": v(-71.65, 24.46) * mm, "mid": v(-70.26, 23.63) * mm, "end": v(-68.66, 23.33) * mm});
            skLineSegment(sketch, "E585", {"start": v(60.65, -42.47) * mm, "end": v(79.33, -34.85) * mm});
            skLineSegment(sketch, "E586", {"start": v(79.33, -34.85) * mm, "end": v(78.9, -36.5) * mm});
            skLineSegment(sketch, "E587", {"start": v(78.9, -36.5) * mm, "end": v(60.37, -44.15) * mm});
            skLineSegment(sketch, "E588", {"start": v(60.37, -44.15) * mm, "end": v(60.65, -42.47) * mm});
            skLineSegment(sketch, "E589", {"start": v(17.15, 2.13) * mm, "end": v(24.79, -2.4) * mm});
            skLineSegment(sketch, "E590", {"start": v(24.79, -2.4) * mm, "end": v(20.1, -9.52) * mm});
            skLineSegment(sketch, "E591", {"start": v(17.15, 2.13) * mm, "end": v(13, -4.75) * mm});
            skLineSegment(sketch, "E592", {"start": v(13, -4.75) * mm, "end": v(20.1, -9.52) * mm});
            skLineSegment(sketch, "E593", {"start": v(5.14, 0.4) * mm, "end": v(12.93, -4.7) * mm});
            skLineSegment(sketch, "E594", {"start": v(5.14, 0.4) * mm, "end": v(0.8, -6.55) * mm});
            skLineSegment(sketch, "E595", {"start": v(0.8, -6.55) * mm, "end": v(8.6, -11.33) * mm});
            skLineSegment(sketch, "E596", {"start": v(38.03, -39.14) * mm, "end": v(44.79, -44.14) * mm});
            skLineSegment(sketch, "E597", {"start": v(44.79, -44.14) * mm, "end": v(41.13, -50.36) * mm});
            skLineSegment(sketch, "E598", {"start": v(38.03, -39.14) * mm, "end": v(34.08, -45.88) * mm});
            skLineSegment(sketch, "E599", {"start": v(34.08, -45.88) * mm, "end": v(41.13, -50.36) * mm});
            skArc(sketch, "E600", {"start": v(-74.73, 16.55) * mm, "mid": v(-75.45, 16.03) * mm, "end": v(-76.15, 15.5) * mm});
            skLineSegment(sketch, "E601", {"start": v(8.6, -11.33) * mm, "end": v(12.93, -4.7) * mm});
            skSolve(sketch);
        }
        {
            var Q0;
            Q0 = qSketchRegion(id + "F2", true);
            extrude(context, id + "F3", {"entities" : qUnion([Q0]), "operationType" : NewBodyOperationType.ADD, "depth" : 4 * mm, "offsetDistance" : 25 * mm});
        }
        {
            var Q0;
            {var subQ6=sQuery(id+"F0.wireOp",EDGE,"E0.left");var subQ7=sQuery(id+"F0.wireOp",EDGE,"E0.top");var subQ8=sQuery(id+"F0.wireOp",EDGE,"E0.right");var subQ9=sQuery(id+"F0.wireOp",EDGE,"E0.bottom");Q0=makeQuery(id+"F3.boolean.opBoolean","SPLIT",FACE,{"disambiguationData":[TD([makeQuery(id+"F1.opExtrude","SWEPT_FACE",FACE,{"disambiguationData":[OSD([subQ9])]})])],"derivedFrom":makeQuery(id+"F1.opExtrude","CAP_FACE",FACE,{"disambiguationData":[OSD([subQ9,subQ7,subQ6,subQ8])],"isStart":true})});}
            var sketch = newSketch(context, id + "F4", { "sketchPlane" : qUnion([Q0])});
            skPoint(sketch, "E602", {"position": v(5.88, 78.93) * mm});
            skPoint(sketch, "E603", {"position": v(60.88, 78.93) * mm});
            skArc(sketch, "E604", {"start": v(5.88, 74.5) * mm, "mid": v(32.18, 62.7) * mm, "end": v(60.88, 59.92) * mm});
            skArc(sketch, "E605", {"start": v(112.49, 40.11) * mm, "mid": v(88.64, 55.1) * mm, "end": v(60.88, 59.92) * mm});
            skPoint(sketch, "E606", {"position": v(5.88, -81.07) * mm});
            skLineSegment(sketch, "E607", {"start": v(5.88, 78.93) * mm, "end": v(5.88, -81.07) * mm, "construction": true});
            skArc(sketch, "E608.MirrorCS", {"start": v(5.88, 74.5) * mm, "mid": v(-20.43, 62.7) * mm, "end": v(-49.12, 59.92) * mm});
            skArc(sketch, "E609.MirrorCS", {"start": v(-100.73, 40.11) * mm, "mid": v(-76.88, 55.1) * mm, "end": v(-49.12, 59.92) * mm});
            skPoint(sketch, "E610", {"position": v(115.88, -1.07) * mm});
            skPoint(sketch, "E611", {"position": v(-104.12, -1.07) * mm});
            skLineSegment(sketch, "E612", {"start": v(-104.12, -1.07) * mm, "end": v(115.88, -1.07) * mm, "construction": true});
            skArc(sketch, "E613.0", {"start": v(-97.3, 36.48) * mm, "mid": v(-75.14, 50.42) * mm, "end": v(-49.34, 54.92) * mm});
            skArc(sketch, "E613.1", {"start": v(5.88, 68.57) * mm, "mid": v(-20.68, 57.47) * mm, "end": v(-49.34, 54.92) * mm});
            skArc(sketch, "E613.2", {"start": v(5.88, 68.57) * mm, "mid": v(32.43, 57.47) * mm, "end": v(61.1, 54.92) * mm});
            skArc(sketch, "E613.3", {"start": v(109.06, 36.48) * mm, "mid": v(86.9, 50.42) * mm, "end": v(61.1, 54.92) * mm});
            skPoint(sketch, "E614", {"position": v(-104.12, 36.9) * mm});
            skArc(sketch, "E615", {"start": v(-104.12, 36.9) * mm, "mid": v(-102.41, 38.5) * mm, "end": v(-100.73, 40.11) * mm});
            skPoint(sketch, "E616", {"position": v(-104.12, 29.43) * mm});
            skArc(sketch, "E617", {"start": v(-97.3, 36.48) * mm, "mid": v(-97.6, 36.2) * mm, "end": v(-97.9, 35.94) * mm});
            skLineSegment(sketch, "E618", {"start": v(-104.12, 36.9) * mm, "end": v(-104.12, 29.43) * mm});
            skArc(sketch, "E619.MirrorCS", {"start": v(115.88, 36.9) * mm, "mid": v(114.16, 38.5) * mm, "end": v(112.49, 40.11) * mm});
            skArc(sketch, "E620.MirrorCS", {"start": v(109.06, 36.48) * mm, "mid": v(109.35, 36.2) * mm, "end": v(109.65, 35.94) * mm});
            skLineSegment(sketch, "E621.MirrorCS", {"start": v(115.88, 36.9) * mm, "end": v(115.88, 29.43) * mm});
            skPoint(sketch, "E622.MirrorP", {"position": v(115.88, 36.9) * mm});
            skPoint(sketch, "E623.MirrorP", {"position": v(115.88, 29.43) * mm});
            skArc(sketch, "E624.MirrorCS", {"start": v(115.88, -39.05) * mm, "mid": v(114.16, -40.64) * mm, "end": v(112.49, -42.26) * mm});
            skLineSegment(sketch, "E625.MirrorCS", {"start": v(-104.12, -39.05) * mm, "end": v(-104.12, -31.58) * mm});
            skArc(sketch, "E626.MirrorCS", {"start": v(-104.12, -39.05) * mm, "mid": v(-102.41, -40.64) * mm, "end": v(-100.73, -42.26) * mm});
            skLineSegment(sketch, "E627.MirrorCS", {"start": v(115.88, -39.05) * mm, "end": v(115.88, -31.58) * mm});
            skArc(sketch, "E628.MirrorCS", {"start": v(109.06, -38.62) * mm, "mid": v(109.35, -38.36) * mm, "end": v(109.65, -38.09) * mm});
            skArc(sketch, "E629.MirrorCS", {"start": v(-97.3, -38.62) * mm, "mid": v(-97.6, -38.36) * mm, "end": v(-97.9, -38.09) * mm});
            skPoint(sketch, "E630.MirrorP", {"position": v(60.88, -81.07) * mm});
            skArc(sketch, "E631.MirrorCS", {"start": v(-97.3, -38.62) * mm, "mid": v(-75.14, -52.57) * mm, "end": v(-49.34, -57.07) * mm});
            skPoint(sketch, "E632.MirrorP", {"position": v(-104.12, -39.05) * mm});
            skArc(sketch, "E633.MirrorCS", {"start": v(109.06, -38.62) * mm, "mid": v(86.9, -52.57) * mm, "end": v(61.1, -57.07) * mm});
            skArc(sketch, "E634.MirrorCS", {"start": v(5.88, -76.65) * mm, "mid": v(-20.43, -64.84) * mm, "end": v(-49.12, -62.06) * mm});
            skArc(sketch, "E635.MirrorCS", {"start": v(5.88, -70.72) * mm, "mid": v(32.43, -59.61) * mm, "end": v(61.1, -57.07) * mm});
            skArc(sketch, "E636.MirrorCS", {"start": v(112.49, -42.26) * mm, "mid": v(88.64, -57.25) * mm, "end": v(60.88, -62.06) * mm});
            skPoint(sketch, "E637.MirrorP", {"position": v(115.88, -39.05) * mm});
            skArc(sketch, "E638.MirrorCS", {"start": v(5.88, -76.65) * mm, "mid": v(32.18, -64.84) * mm, "end": v(60.88, -62.06) * mm});
            skPoint(sketch, "E639.MirrorP", {"position": v(-104.12, -31.58) * mm});
            skArc(sketch, "E640.MirrorCS", {"start": v(-100.73, -42.26) * mm, "mid": v(-76.88, -57.25) * mm, "end": v(-49.12, -62.06) * mm});
            skArc(sketch, "E641.MirrorCS", {"start": v(5.88, -70.72) * mm, "mid": v(-20.68, -59.61) * mm, "end": v(-49.34, -57.07) * mm});
            skPoint(sketch, "E642.MirrorP", {"position": v(115.88, -31.58) * mm});
            skArc(sketch, "E643", {"start": v(109.65, -38.09) * mm, "mid": v(111.01, -1.07) * mm, "end": v(109.65, 35.94) * mm});
            skLineSegment(sketch, "E644", {"start": v(115.88, 36.9) * mm, "end": v(115.88, -39.05) * mm});
            skPoint(sketch, "E645.orphan", {"position": v(109.06, 43.15) * mm});
            skPoint(sketch, "E646.orphan", {"position": v(109.06, -45.3) * mm});
            skArc(sketch, "E647.MirrorCS", {"start": v(-97.9, -38.09) * mm, "mid": v(-99.26, -1.07) * mm, "end": v(-97.9, 35.94) * mm});
            skLineSegment(sketch, "E648.MirrorCS", {"start": v(-104.12, 36.9) * mm, "end": v(-104.12, -39.05) * mm});
            skSolve(sketch);
        }
        {
            var Q0;
            Q0 = qSketchRegion(id + "F4", true);
            extrude(context, id + "F5", {"entities" : qUnion([Q0]), "operationType" : NewBodyOperationType.ADD, "depth" : 5 * mm, "offsetDistance" : 25 * mm});
        }
        {
            var Q0;
            Q0=makeQuery(id+"F1.opExtrude","SWEPT_EDGE",EDGE,{"disambiguationData":[OSD([sQuery(id+"F0.wireOp",EDGE,"E0.bottom"),sQuery(id+"F0.wireOp",EDGE,"E0.left")])]});
            var Q1;
            Q1=makeQuery(id+"F1.opExtrude","SWEPT_EDGE",EDGE,{"disambiguationData":[OSD([sQuery(id+"F0.wireOp",EDGE,"E0.bottom"),sQuery(id+"F0.wireOp",EDGE,"E0.right")])]});
            var Q2;
            Q2=makeQuery(id+"F1.opExtrude","SWEPT_EDGE",EDGE,{"disambiguationData":[OSD([sQuery(id+"F0.wireOp",EDGE,"E0.top"),sQuery(id+"F0.wireOp",EDGE,"E0.right")])]});
            var Q3;
            Q3=makeQuery(id+"F1.opExtrude","SWEPT_EDGE",EDGE,{"disambiguationData":[OSD([sQuery(id+"F0.wireOp",EDGE,"E0.top"),sQuery(id+"F0.wireOp",EDGE,"E0.left")])]});
            chamfer(context, id + "F6", {"entities" : qUnion([Q0, Q1, Q2, Q3]), "chamferType" : ChamferType.OFFSET_ANGLE, "width" : 30 * mm, "oppositeDirection" : false, "angle" : 30 * degree, "tangentPropagation" : true});
        }
    });
